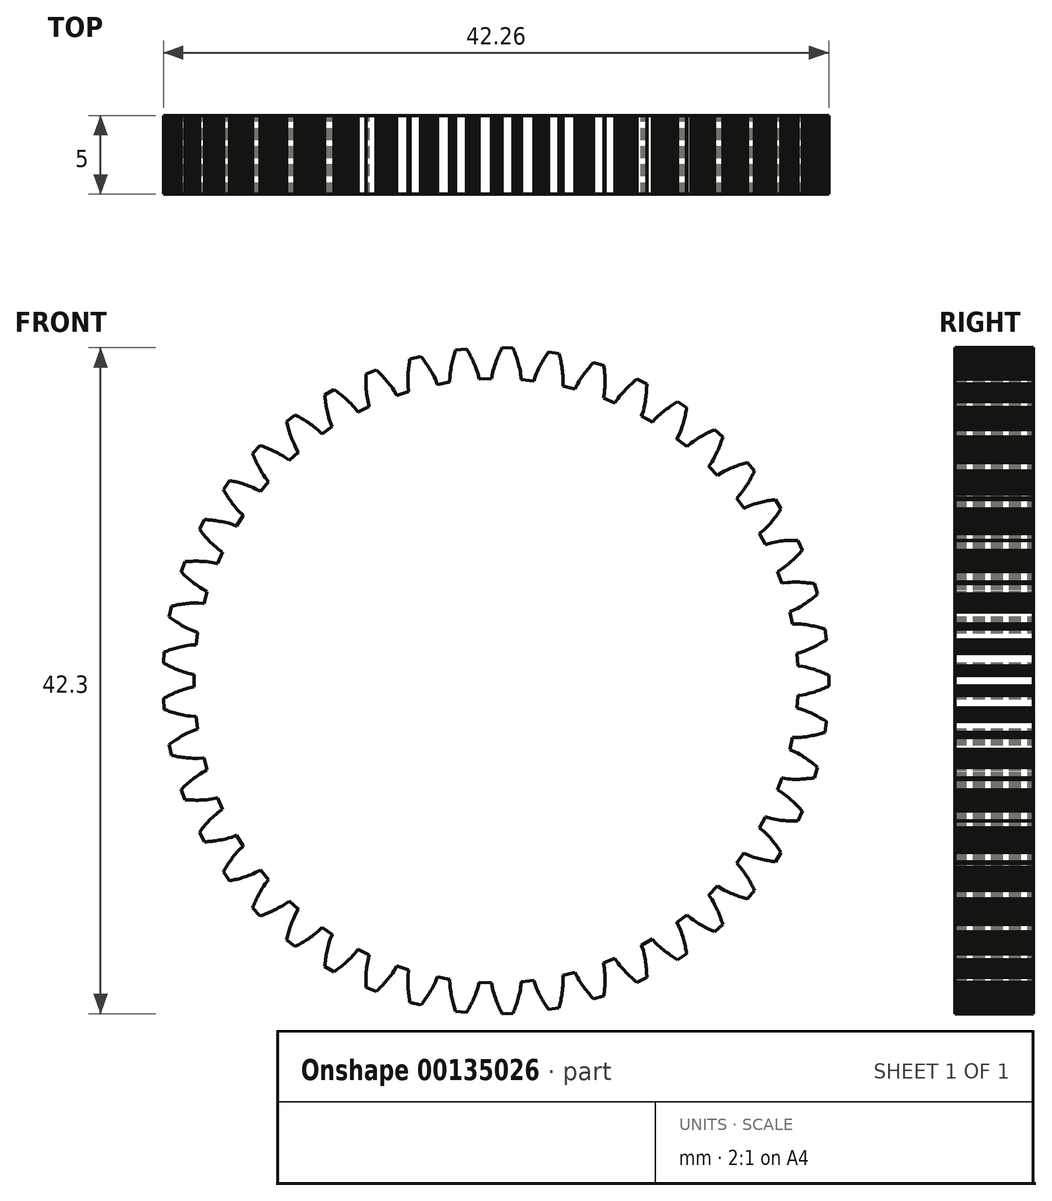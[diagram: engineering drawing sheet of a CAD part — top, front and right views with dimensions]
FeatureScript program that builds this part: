
annotation { "Feature Type Name" : "Feature", "Feature Type Description" : "" }
export const myFeature = defineFeature(function(context is Context, id is Id, definition is map)
    precondition{}
    {
        {
            var Q0;
            Q0=qCreatedBy(makeId("Front.planeOp"),FACE);
            var sketch = newSketch(context, id + "F0", { "sketchPlane" : qUnion([Q0])});
            skLineSegment(sketch, "E0", {"start": v(19.15, -0.94) * mm, "end": v(19.17, -0.94) * mm});
            skLineSegment(sketch, "E1", {"start": v(19.17, -0.94) * mm, "end": v(19.5, -0.9) * mm});
            skLineSegment(sketch, "E2", {"start": v(19.5, -0.9) * mm, "end": v(19.67, -0.86) * mm});
            skLineSegment(sketch, "E3", {"start": v(19.67, -0.86) * mm, "end": v(19.83, -0.82) * mm});
            skLineSegment(sketch, "E4", {"start": v(19.83, -0.82) * mm, "end": v(19.97, -0.78) * mm});
            skLineSegment(sketch, "E5", {"start": v(19.97, -0.78) * mm, "end": v(20.1, -0.74) * mm});
            skLineSegment(sketch, "E6", {"start": v(20.1, -0.74) * mm, "end": v(20.23, -0.7) * mm});
            skLineSegment(sketch, "E7", {"start": v(20.23, -0.7) * mm, "end": v(20.36, -0.66) * mm});
            skLineSegment(sketch, "E8", {"start": v(20.36, -0.66) * mm, "end": v(20.47, -0.62) * mm});
            skLineSegment(sketch, "E9", {"start": v(20.47, -0.62) * mm, "end": v(20.6, -0.58) * mm});
            skLineSegment(sketch, "E10", {"start": v(20.6, -0.58) * mm, "end": v(20.7, -0.53) * mm});
            skLineSegment(sketch, "E11", {"start": v(20.7, -0.53) * mm, "end": v(20.81, -0.49) * mm});
            skLineSegment(sketch, "E12", {"start": v(20.81, -0.49) * mm, "end": v(20.92, -0.44) * mm});
            skLineSegment(sketch, "E13", {"start": v(20.92, -0.44) * mm, "end": v(21.03, -0.4) * mm});
            skLineSegment(sketch, "E14", {"start": v(21.03, -0.4) * mm, "end": v(21.13, -0.35) * mm});
            skLineSegment(sketch, "E15", {"start": v(21.13, -0.35) * mm, "end": v(21.13, 0.35) * mm});
            skLineSegment(sketch, "E16", {"start": v(21.13, 0.35) * mm, "end": v(21.03, 0.4) * mm});
            skLineSegment(sketch, "E17", {"start": v(21.03, 0.4) * mm, "end": v(20.92, 0.44) * mm});
            skLineSegment(sketch, "E18", {"start": v(20.92, 0.44) * mm, "end": v(20.81, 0.49) * mm});
            skLineSegment(sketch, "E19", {"start": v(20.81, 0.49) * mm, "end": v(20.7, 0.53) * mm});
            skLineSegment(sketch, "E20", {"start": v(20.7, 0.53) * mm, "end": v(20.6, 0.58) * mm});
            skLineSegment(sketch, "E21", {"start": v(20.6, 0.58) * mm, "end": v(20.47, 0.62) * mm});
            skLineSegment(sketch, "E22", {"start": v(20.47, 0.62) * mm, "end": v(20.36, 0.66) * mm});
            skLineSegment(sketch, "E23", {"start": v(20.36, 0.66) * mm, "end": v(20.23, 0.7) * mm});
            skLineSegment(sketch, "E24", {"start": v(20.23, 0.7) * mm, "end": v(20.1, 0.74) * mm});
            skLineSegment(sketch, "E25", {"start": v(20.1, 0.74) * mm, "end": v(19.97, 0.78) * mm});
            skLineSegment(sketch, "E26", {"start": v(19.97, 0.78) * mm, "end": v(19.83, 0.82) * mm});
            skLineSegment(sketch, "E27", {"start": v(19.83, 0.82) * mm, "end": v(19.67, 0.86) * mm});
            skLineSegment(sketch, "E28", {"start": v(19.67, 0.86) * mm, "end": v(19.5, 0.9) * mm});
            skLineSegment(sketch, "E29", {"start": v(19.5, 0.9) * mm, "end": v(19.17, 0.94) * mm});
            skLineSegment(sketch, "E30", {"start": v(19.17, 0.94) * mm, "end": v(19.15, 0.94) * mm});
            skLineSegment(sketch, "E31", {"start": v(19.15, 0.94) * mm, "end": v(19.1, 1.74) * mm});
            skLineSegment(sketch, "E32", {"start": v(19.1, 1.74) * mm, "end": v(19.12, 1.74) * mm});
            skLineSegment(sketch, "E33", {"start": v(19.12, 1.74) * mm, "end": v(19.43, 1.83) * mm});
            skLineSegment(sketch, "E34", {"start": v(19.43, 1.83) * mm, "end": v(19.6, 1.89) * mm});
            skLineSegment(sketch, "E35", {"start": v(19.6, 1.89) * mm, "end": v(19.75, 1.95) * mm});
            skLineSegment(sketch, "E36", {"start": v(19.75, 1.95) * mm, "end": v(19.89, 2) * mm});
            skLineSegment(sketch, "E37", {"start": v(19.89, 2) * mm, "end": v(20.01, 2.06) * mm});
            skLineSegment(sketch, "E38", {"start": v(20.01, 2.06) * mm, "end": v(20.13, 2.12) * mm});
            skLineSegment(sketch, "E39", {"start": v(20.13, 2.12) * mm, "end": v(20.25, 2.18) * mm});
            skLineSegment(sketch, "E40", {"start": v(20.25, 2.18) * mm, "end": v(20.36, 2.24) * mm});
            skLineSegment(sketch, "E41", {"start": v(20.36, 2.24) * mm, "end": v(20.47, 2.3) * mm});
            skLineSegment(sketch, "E42", {"start": v(20.47, 2.3) * mm, "end": v(20.58, 2.36) * mm});
            skLineSegment(sketch, "E43", {"start": v(20.58, 2.36) * mm, "end": v(20.68, 2.42) * mm});
            skLineSegment(sketch, "E44", {"start": v(20.68, 2.42) * mm, "end": v(20.78, 2.48) * mm});
            skLineSegment(sketch, "E45", {"start": v(20.78, 2.48) * mm, "end": v(20.88, 2.54) * mm});
            skLineSegment(sketch, "E46", {"start": v(20.88, 2.54) * mm, "end": v(20.98, 2.6) * mm});
            skLineSegment(sketch, "E47", {"start": v(20.98, 2.6) * mm, "end": v(20.88, 3.29) * mm});
            skLineSegment(sketch, "E48", {"start": v(20.88, 3.29) * mm, "end": v(20.77, 3.32) * mm});
            skLineSegment(sketch, "E49", {"start": v(20.77, 3.32) * mm, "end": v(20.66, 3.35) * mm});
            skLineSegment(sketch, "E50", {"start": v(20.66, 3.35) * mm, "end": v(20.54, 3.38) * mm});
            skLineSegment(sketch, "E51", {"start": v(20.54, 3.38) * mm, "end": v(20.43, 3.41) * mm});
            skLineSegment(sketch, "E52", {"start": v(20.43, 3.41) * mm, "end": v(20.3, 3.44) * mm});
            skLineSegment(sketch, "E53", {"start": v(20.3, 3.44) * mm, "end": v(20.19, 3.47) * mm});
            skLineSegment(sketch, "E54", {"start": v(20.19, 3.47) * mm, "end": v(20.07, 3.5) * mm});
            skLineSegment(sketch, "E55", {"start": v(20.07, 3.5) * mm, "end": v(19.94, 3.51) * mm});
            skLineSegment(sketch, "E56", {"start": v(19.94, 3.51) * mm, "end": v(19.8, 3.54) * mm});
            skLineSegment(sketch, "E57", {"start": v(19.8, 3.54) * mm, "end": v(19.67, 3.56) * mm});
            skLineSegment(sketch, "E58", {"start": v(19.67, 3.56) * mm, "end": v(19.52, 3.58) * mm});
            skLineSegment(sketch, "E59", {"start": v(19.52, 3.58) * mm, "end": v(19.36, 3.6) * mm});
            skLineSegment(sketch, "E60", {"start": v(19.36, 3.6) * mm, "end": v(19.18, 3.6) * mm});
            skLineSegment(sketch, "E61", {"start": v(19.18, 3.6) * mm, "end": v(18.85, 3.6) * mm});
            skLineSegment(sketch, "E62", {"start": v(18.85, 3.6) * mm, "end": v(18.84, 3.6) * mm});
            skLineSegment(sketch, "E63", {"start": v(18.84, 3.6) * mm, "end": v(18.67, 4.38) * mm});
            skLineSegment(sketch, "E64", {"start": v(18.67, 4.38) * mm, "end": v(18.69, 4.38) * mm});
            skLineSegment(sketch, "E65", {"start": v(18.69, 4.38) * mm, "end": v(18.99, 4.52) * mm});
            skLineSegment(sketch, "E66", {"start": v(18.99, 4.52) * mm, "end": v(19.15, 4.6) * mm});
            skLineSegment(sketch, "E67", {"start": v(19.15, 4.6) * mm, "end": v(19.29, 4.68) * mm});
            skLineSegment(sketch, "E68", {"start": v(19.29, 4.68) * mm, "end": v(19.41, 4.76) * mm});
            skLineSegment(sketch, "E69", {"start": v(19.41, 4.76) * mm, "end": v(19.53, 4.83) * mm});
            skLineSegment(sketch, "E70", {"start": v(19.53, 4.83) * mm, "end": v(19.64, 4.9) * mm});
            skLineSegment(sketch, "E71", {"start": v(19.64, 4.9) * mm, "end": v(19.75, 4.98) * mm});
            skLineSegment(sketch, "E72", {"start": v(19.75, 4.98) * mm, "end": v(19.85, 5.05) * mm});
            skLineSegment(sketch, "E73", {"start": v(19.85, 5.05) * mm, "end": v(19.95, 5.12) * mm});
            skLineSegment(sketch, "E74", {"start": v(19.95, 5.12) * mm, "end": v(20.05, 5.2) * mm});
            skLineSegment(sketch, "E75", {"start": v(20.05, 5.2) * mm, "end": v(20.14, 5.27) * mm});
            skLineSegment(sketch, "E76", {"start": v(20.14, 5.27) * mm, "end": v(20.23, 5.35) * mm});
            skLineSegment(sketch, "E77", {"start": v(20.23, 5.35) * mm, "end": v(20.32, 5.42) * mm});
            skLineSegment(sketch, "E78", {"start": v(20.32, 5.42) * mm, "end": v(20.4, 5.5) * mm});
            skLineSegment(sketch, "E79", {"start": v(20.4, 5.5) * mm, "end": v(20.22, 6.16) * mm});
            skLineSegment(sketch, "E80", {"start": v(20.22, 6.16) * mm, "end": v(20.1, 6.18) * mm});
            skLineSegment(sketch, "E81", {"start": v(20.1, 6.18) * mm, "end": v(20, 6.2) * mm});
            skLineSegment(sketch, "E82", {"start": v(20, 6.2) * mm, "end": v(19.87, 6.2) * mm});
            skLineSegment(sketch, "E83", {"start": v(19.87, 6.2) * mm, "end": v(19.75, 6.22) * mm});
            skLineSegment(sketch, "E84", {"start": v(19.75, 6.22) * mm, "end": v(19.63, 6.23) * mm});
            skLineSegment(sketch, "E85", {"start": v(19.63, 6.23) * mm, "end": v(19.5, 6.24) * mm});
            skLineSegment(sketch, "E86", {"start": v(19.5, 6.24) * mm, "end": v(19.38, 6.25) * mm});
            skLineSegment(sketch, "E87", {"start": v(19.38, 6.25) * mm, "end": v(19.25, 6.26) * mm});
            skLineSegment(sketch, "E88", {"start": v(19.25, 6.26) * mm, "end": v(19.12, 6.26) * mm});
            skLineSegment(sketch, "E89", {"start": v(19.12, 6.26) * mm, "end": v(18.98, 6.26) * mm});
            skLineSegment(sketch, "E90", {"start": v(18.98, 6.26) * mm, "end": v(18.83, 6.26) * mm});
            skLineSegment(sketch, "E91", {"start": v(18.83, 6.26) * mm, "end": v(18.67, 6.25) * mm});
            skLineSegment(sketch, "E92", {"start": v(18.67, 6.25) * mm, "end": v(18.5, 6.24) * mm});
            skLineSegment(sketch, "E93", {"start": v(18.5, 6.24) * mm, "end": v(18.17, 6.2) * mm});
            skLineSegment(sketch, "E94", {"start": v(18.17, 6.2) * mm, "end": v(18.15, 6.19) * mm});
            skLineSegment(sketch, "E95", {"start": v(18.15, 6.19) * mm, "end": v(17.88, 6.94) * mm});
            skLineSegment(sketch, "E96", {"start": v(17.88, 6.94) * mm, "end": v(17.9, 6.94) * mm});
            skLineSegment(sketch, "E97", {"start": v(17.9, 6.94) * mm, "end": v(18.17, 7.12) * mm});
            skLineSegment(sketch, "E98", {"start": v(18.17, 7.12) * mm, "end": v(18.32, 7.22) * mm});
            skLineSegment(sketch, "E99", {"start": v(18.32, 7.22) * mm, "end": v(18.45, 7.32) * mm});
            skLineSegment(sketch, "E100", {"start": v(18.45, 7.32) * mm, "end": v(18.56, 7.41) * mm});
            skLineSegment(sketch, "E101", {"start": v(18.56, 7.41) * mm, "end": v(18.67, 7.5) * mm});
            skLineSegment(sketch, "E102", {"start": v(18.67, 7.5) * mm, "end": v(18.77, 7.6) * mm});
            skLineSegment(sketch, "E103", {"start": v(18.77, 7.6) * mm, "end": v(18.86, 7.68) * mm});
            skLineSegment(sketch, "E104", {"start": v(18.86, 7.68) * mm, "end": v(18.96, 7.77) * mm});
            skLineSegment(sketch, "E105", {"start": v(18.96, 7.77) * mm, "end": v(19.04, 7.85) * mm});
            skLineSegment(sketch, "E106", {"start": v(19.04, 7.85) * mm, "end": v(19.13, 7.94) * mm});
            skLineSegment(sketch, "E107", {"start": v(19.13, 7.94) * mm, "end": v(19.21, 8.03) * mm});
            skLineSegment(sketch, "E108", {"start": v(19.21, 8.03) * mm, "end": v(19.3, 8.11) * mm});
            skLineSegment(sketch, "E109", {"start": v(19.3, 8.11) * mm, "end": v(19.37, 8.2) * mm});
            skLineSegment(sketch, "E110", {"start": v(19.37, 8.2) * mm, "end": v(19.45, 8.29) * mm});
            skLineSegment(sketch, "E111", {"start": v(19.45, 8.29) * mm, "end": v(19.16, 8.92) * mm});
            skLineSegment(sketch, "E112", {"start": v(19.16, 8.92) * mm, "end": v(19.05, 8.92) * mm});
            skLineSegment(sketch, "E113", {"start": v(19.05, 8.92) * mm, "end": v(18.93, 8.92) * mm});
            skLineSegment(sketch, "E114", {"start": v(18.93, 8.92) * mm, "end": v(18.82, 8.92) * mm});
            skLineSegment(sketch, "E115", {"start": v(18.82, 8.92) * mm, "end": v(18.7, 8.91) * mm});
            skLineSegment(sketch, "E116", {"start": v(18.7, 8.91) * mm, "end": v(18.57, 8.9) * mm});
            skLineSegment(sketch, "E117", {"start": v(18.57, 8.9) * mm, "end": v(18.45, 8.9) * mm});
            skLineSegment(sketch, "E118", {"start": v(18.45, 8.9) * mm, "end": v(18.32, 8.9) * mm});
            skLineSegment(sketch, "E119", {"start": v(18.32, 8.9) * mm, "end": v(18.2, 8.88) * mm});
            skLineSegment(sketch, "E120", {"start": v(18.2, 8.88) * mm, "end": v(18.06, 8.86) * mm});
            skLineSegment(sketch, "E121", {"start": v(18.06, 8.86) * mm, "end": v(17.92, 8.84) * mm});
            skLineSegment(sketch, "E122", {"start": v(17.92, 8.84) * mm, "end": v(17.78, 8.82) * mm});
            skLineSegment(sketch, "E123", {"start": v(17.78, 8.82) * mm, "end": v(17.62, 8.8) * mm});
            skLineSegment(sketch, "E124", {"start": v(17.62, 8.8) * mm, "end": v(17.44, 8.75) * mm});
            skLineSegment(sketch, "E125", {"start": v(17.44, 8.75) * mm, "end": v(17.13, 8.66) * mm});
            skLineSegment(sketch, "E126", {"start": v(17.13, 8.66) * mm, "end": v(17.11, 8.65) * mm});
            skLineSegment(sketch, "E127", {"start": v(17.11, 8.65) * mm, "end": v(16.74, 9.36) * mm});
            skLineSegment(sketch, "E128", {"start": v(16.74, 9.36) * mm, "end": v(16.75, 9.37) * mm});
            skLineSegment(sketch, "E129", {"start": v(16.75, 9.37) * mm, "end": v(17, 9.58) * mm});
            skLineSegment(sketch, "E130", {"start": v(17, 9.58) * mm, "end": v(17.14, 9.7) * mm});
            skLineSegment(sketch, "E131", {"start": v(17.14, 9.7) * mm, "end": v(17.25, 9.82) * mm});
            skLineSegment(sketch, "E132", {"start": v(17.25, 9.82) * mm, "end": v(17.35, 9.93) * mm});
            skLineSegment(sketch, "E133", {"start": v(17.35, 9.93) * mm, "end": v(17.44, 10.03) * mm});
            skLineSegment(sketch, "E134", {"start": v(17.44, 10.03) * mm, "end": v(17.53, 10.13) * mm});
            skLineSegment(sketch, "E135", {"start": v(17.53, 10.13) * mm, "end": v(17.61, 10.23) * mm});
            skLineSegment(sketch, "E136", {"start": v(17.61, 10.23) * mm, "end": v(17.69, 10.33) * mm});
            skLineSegment(sketch, "E137", {"start": v(17.69, 10.33) * mm, "end": v(17.77, 10.43) * mm});
            skLineSegment(sketch, "E138", {"start": v(17.77, 10.43) * mm, "end": v(17.84, 10.53) * mm});
            skLineSegment(sketch, "E139", {"start": v(17.84, 10.53) * mm, "end": v(17.9, 10.62) * mm});
            skLineSegment(sketch, "E140", {"start": v(17.9, 10.62) * mm, "end": v(17.97, 10.72) * mm});
            skLineSegment(sketch, "E141", {"start": v(17.97, 10.72) * mm, "end": v(18.04, 10.82) * mm});
            skLineSegment(sketch, "E142", {"start": v(18.04, 10.82) * mm, "end": v(18.1, 10.91) * mm});
            skLineSegment(sketch, "E143", {"start": v(18.1, 10.91) * mm, "end": v(17.74, 11.5) * mm});
            skLineSegment(sketch, "E144", {"start": v(17.74, 11.5) * mm, "end": v(17.62, 11.48) * mm});
            skLineSegment(sketch, "E145", {"start": v(17.62, 11.48) * mm, "end": v(17.5, 11.47) * mm});
            skLineSegment(sketch, "E146", {"start": v(17.5, 11.47) * mm, "end": v(17.4, 11.45) * mm});
            skLineSegment(sketch, "E147", {"start": v(17.4, 11.45) * mm, "end": v(17.27, 11.43) * mm});
            skLineSegment(sketch, "E148", {"start": v(17.27, 11.43) * mm, "end": v(17.15, 11.4) * mm});
            skLineSegment(sketch, "E149", {"start": v(17.15, 11.4) * mm, "end": v(17.03, 11.38) * mm});
            skLineSegment(sketch, "E150", {"start": v(17.03, 11.38) * mm, "end": v(16.9, 11.36) * mm});
            skLineSegment(sketch, "E151", {"start": v(16.9, 11.36) * mm, "end": v(16.78, 11.33) * mm});
            skLineSegment(sketch, "E152", {"start": v(16.78, 11.33) * mm, "end": v(16.65, 11.3) * mm});
            skLineSegment(sketch, "E153", {"start": v(16.65, 11.3) * mm, "end": v(16.52, 11.25) * mm});
            skLineSegment(sketch, "E154", {"start": v(16.52, 11.25) * mm, "end": v(16.38, 11.21) * mm});
            skLineSegment(sketch, "E155", {"start": v(16.38, 11.21) * mm, "end": v(16.23, 11.16) * mm});
            skLineSegment(sketch, "E156", {"start": v(16.23, 11.16) * mm, "end": v(16.06, 11.1) * mm});
            skLineSegment(sketch, "E157", {"start": v(16.06, 11.1) * mm, "end": v(15.76, 10.96) * mm});
            skLineSegment(sketch, "E158", {"start": v(15.76, 10.96) * mm, "end": v(15.74, 10.95) * mm});
            skLineSegment(sketch, "E159", {"start": v(15.74, 10.95) * mm, "end": v(15.27, 11.6) * mm});
            skLineSegment(sketch, "E160", {"start": v(15.27, 11.6) * mm, "end": v(15.29, 11.61) * mm});
            skLineSegment(sketch, "E161", {"start": v(15.29, 11.61) * mm, "end": v(15.5, 11.85) * mm});
            skLineSegment(sketch, "E162", {"start": v(15.5, 11.85) * mm, "end": v(15.62, 12) * mm});
            skLineSegment(sketch, "E163", {"start": v(15.62, 12) * mm, "end": v(15.71, 12.13) * mm});
            skLineSegment(sketch, "E164", {"start": v(15.71, 12.13) * mm, "end": v(15.8, 12.25) * mm});
            skLineSegment(sketch, "E165", {"start": v(15.8, 12.25) * mm, "end": v(15.88, 12.36) * mm});
            skLineSegment(sketch, "E166", {"start": v(15.88, 12.36) * mm, "end": v(15.95, 12.47) * mm});
            skLineSegment(sketch, "E167", {"start": v(15.95, 12.47) * mm, "end": v(16.02, 12.59) * mm});
            skLineSegment(sketch, "E168", {"start": v(16.02, 12.59) * mm, "end": v(16.08, 12.7) * mm});
            skLineSegment(sketch, "E169", {"start": v(16.08, 12.7) * mm, "end": v(16.14, 12.8) * mm});
            skLineSegment(sketch, "E170", {"start": v(16.14, 12.8) * mm, "end": v(16.2, 12.9) * mm});
            skLineSegment(sketch, "E171", {"start": v(16.2, 12.9) * mm, "end": v(16.25, 13.01) * mm});
            skLineSegment(sketch, "E172", {"start": v(16.25, 13.01) * mm, "end": v(16.3, 13.12) * mm});
            skLineSegment(sketch, "E173", {"start": v(16.3, 13.12) * mm, "end": v(16.36, 13.22) * mm});
            skLineSegment(sketch, "E174", {"start": v(16.36, 13.22) * mm, "end": v(16.4, 13.33) * mm});
            skLineSegment(sketch, "E175", {"start": v(16.4, 13.33) * mm, "end": v(15.96, 13.86) * mm});
            skLineSegment(sketch, "E176", {"start": v(15.96, 13.86) * mm, "end": v(15.85, 13.83) * mm});
            skLineSegment(sketch, "E177", {"start": v(15.85, 13.83) * mm, "end": v(15.74, 13.8) * mm});
            skLineSegment(sketch, "E178", {"start": v(15.74, 13.8) * mm, "end": v(15.63, 13.76) * mm});
            skLineSegment(sketch, "E179", {"start": v(15.63, 13.76) * mm, "end": v(15.51, 13.72) * mm});
            skLineSegment(sketch, "E180", {"start": v(15.51, 13.72) * mm, "end": v(15.4, 13.69) * mm});
            skLineSegment(sketch, "E181", {"start": v(15.4, 13.69) * mm, "end": v(15.28, 13.64) * mm});
            skLineSegment(sketch, "E182", {"start": v(15.28, 13.64) * mm, "end": v(15.16, 13.6) * mm});
            skLineSegment(sketch, "E183", {"start": v(15.16, 13.6) * mm, "end": v(15.04, 13.55) * mm});
            skLineSegment(sketch, "E184", {"start": v(15.04, 13.55) * mm, "end": v(14.92, 13.5) * mm});
            skLineSegment(sketch, "E185", {"start": v(14.92, 13.5) * mm, "end": v(14.8, 13.45) * mm});
            skLineSegment(sketch, "E186", {"start": v(14.8, 13.45) * mm, "end": v(14.66, 13.38) * mm});
            skLineSegment(sketch, "E187", {"start": v(14.66, 13.38) * mm, "end": v(14.52, 13.31) * mm});
            skLineSegment(sketch, "E188", {"start": v(14.52, 13.31) * mm, "end": v(14.36, 13.23) * mm});
            skLineSegment(sketch, "E189", {"start": v(14.36, 13.23) * mm, "end": v(14.08, 13.05) * mm});
            skLineSegment(sketch, "E190", {"start": v(14.08, 13.05) * mm, "end": v(14.07, 13.04) * mm});
            skLineSegment(sketch, "E191", {"start": v(14.07, 13.04) * mm, "end": v(13.5, 13.62) * mm});
            skLineSegment(sketch, "E192", {"start": v(13.5, 13.62) * mm, "end": v(13.52, 13.63) * mm});
            skLineSegment(sketch, "E193", {"start": v(13.52, 13.63) * mm, "end": v(13.7, 13.9) * mm});
            skLineSegment(sketch, "E194", {"start": v(13.7, 13.9) * mm, "end": v(13.8, 14.06) * mm});
            skLineSegment(sketch, "E195", {"start": v(13.8, 14.06) * mm, "end": v(13.87, 14.2) * mm});
            skLineSegment(sketch, "E196", {"start": v(13.87, 14.2) * mm, "end": v(13.94, 14.33) * mm});
            skLineSegment(sketch, "E197", {"start": v(13.94, 14.33) * mm, "end": v(14, 14.45) * mm});
            skLineSegment(sketch, "E198", {"start": v(14, 14.45) * mm, "end": v(14.06, 14.57) * mm});
            skLineSegment(sketch, "E199", {"start": v(14.06, 14.57) * mm, "end": v(14.1, 14.7) * mm});
            skLineSegment(sketch, "E200", {"start": v(14.1, 14.7) * mm, "end": v(14.16, 14.81) * mm});
            skLineSegment(sketch, "E201", {"start": v(14.16, 14.81) * mm, "end": v(14.2, 14.93) * mm});
            skLineSegment(sketch, "E202", {"start": v(14.2, 14.93) * mm, "end": v(14.24, 15.04) * mm});
            skLineSegment(sketch, "E203", {"start": v(14.24, 15.04) * mm, "end": v(14.28, 15.15) * mm});
            skLineSegment(sketch, "E204", {"start": v(14.28, 15.15) * mm, "end": v(14.32, 15.26) * mm});
            skLineSegment(sketch, "E205", {"start": v(14.32, 15.26) * mm, "end": v(14.36, 15.37) * mm});
            skLineSegment(sketch, "E206", {"start": v(14.36, 15.37) * mm, "end": v(14.4, 15.48) * mm});
            skLineSegment(sketch, "E207", {"start": v(14.4, 15.48) * mm, "end": v(13.88, 15.95) * mm});
            skLineSegment(sketch, "E208", {"start": v(13.88, 15.95) * mm, "end": v(13.77, 15.9) * mm});
            skLineSegment(sketch, "E209", {"start": v(13.77, 15.9) * mm, "end": v(13.67, 15.85) * mm});
            skLineSegment(sketch, "E210", {"start": v(13.67, 15.85) * mm, "end": v(13.56, 15.8) * mm});
            skLineSegment(sketch, "E211", {"start": v(13.56, 15.8) * mm, "end": v(13.45, 15.75) * mm});
            skLineSegment(sketch, "E212", {"start": v(13.45, 15.75) * mm, "end": v(13.34, 15.7) * mm});
            skLineSegment(sketch, "E213", {"start": v(13.34, 15.7) * mm, "end": v(13.23, 15.64) * mm});
            skLineSegment(sketch, "E214", {"start": v(13.23, 15.64) * mm, "end": v(13.12, 15.58) * mm});
            skLineSegment(sketch, "E215", {"start": v(13.12, 15.58) * mm, "end": v(13.01, 15.52) * mm});
            skLineSegment(sketch, "E216", {"start": v(13.01, 15.52) * mm, "end": v(12.9, 15.45) * mm});
            skLineSegment(sketch, "E217", {"start": v(12.9, 15.45) * mm, "end": v(12.78, 15.38) * mm});
            skLineSegment(sketch, "E218", {"start": v(12.78, 15.38) * mm, "end": v(12.65, 15.3) * mm});
            skLineSegment(sketch, "E219", {"start": v(12.65, 15.3) * mm, "end": v(12.52, 15.2) * mm});
            skLineSegment(sketch, "E220", {"start": v(12.52, 15.2) * mm, "end": v(12.37, 15.1) * mm});
            skLineSegment(sketch, "E221", {"start": v(12.37, 15.1) * mm, "end": v(12.13, 14.89) * mm});
            skLineSegment(sketch, "E222", {"start": v(12.13, 14.89) * mm, "end": v(12.11, 14.87) * mm});
            skLineSegment(sketch, "E223", {"start": v(12.11, 14.87) * mm, "end": v(11.48, 15.36) * mm});
            skLineSegment(sketch, "E224", {"start": v(11.48, 15.36) * mm, "end": v(11.5, 15.38) * mm});
            skLineSegment(sketch, "E225", {"start": v(11.5, 15.38) * mm, "end": v(11.64, 15.67) * mm});
            skLineSegment(sketch, "E226", {"start": v(11.64, 15.67) * mm, "end": v(11.7, 15.84) * mm});
            skLineSegment(sketch, "E227", {"start": v(11.7, 15.84) * mm, "end": v(11.76, 16) * mm});
            skLineSegment(sketch, "E228", {"start": v(11.76, 16) * mm, "end": v(11.81, 16.13) * mm});
            skLineSegment(sketch, "E229", {"start": v(11.81, 16.13) * mm, "end": v(11.85, 16.26) * mm});
            skLineSegment(sketch, "E230", {"start": v(11.85, 16.26) * mm, "end": v(11.9, 16.4) * mm});
            skLineSegment(sketch, "E231", {"start": v(11.9, 16.4) * mm, "end": v(11.93, 16.52) * mm});
            skLineSegment(sketch, "E232", {"start": v(11.93, 16.52) * mm, "end": v(11.96, 16.64) * mm});
            skLineSegment(sketch, "E233", {"start": v(11.96, 16.64) * mm, "end": v(11.99, 16.76) * mm});
            skLineSegment(sketch, "E234", {"start": v(11.99, 16.76) * mm, "end": v(12.01, 16.88) * mm});
            skLineSegment(sketch, "E235", {"start": v(12.01, 16.88) * mm, "end": v(12.04, 17) * mm});
            skLineSegment(sketch, "E236", {"start": v(12.04, 17) * mm, "end": v(12.06, 17.11) * mm});
            skLineSegment(sketch, "E237", {"start": v(12.06, 17.11) * mm, "end": v(12.08, 17.23) * mm});
            skLineSegment(sketch, "E238", {"start": v(12.08, 17.23) * mm, "end": v(12.1, 17.34) * mm});
            skLineSegment(sketch, "E239", {"start": v(12.1, 17.34) * mm, "end": v(11.53, 17.73) * mm});
            skLineSegment(sketch, "E240", {"start": v(11.53, 17.73) * mm, "end": v(11.43, 17.67) * mm});
            skLineSegment(sketch, "E241", {"start": v(11.43, 17.67) * mm, "end": v(11.33, 17.6) * mm});
            skLineSegment(sketch, "E242", {"start": v(11.33, 17.6) * mm, "end": v(11.23, 17.54) * mm});
            skLineSegment(sketch, "E243", {"start": v(11.23, 17.54) * mm, "end": v(11.13, 17.47) * mm});
            skLineSegment(sketch, "E244", {"start": v(11.13, 17.47) * mm, "end": v(11.03, 17.4) * mm});
            skLineSegment(sketch, "E245", {"start": v(11.03, 17.4) * mm, "end": v(10.93, 17.33) * mm});
            skLineSegment(sketch, "E246", {"start": v(10.93, 17.33) * mm, "end": v(10.83, 17.26) * mm});
            skLineSegment(sketch, "E247", {"start": v(10.83, 17.26) * mm, "end": v(10.72, 17.18) * mm});
            skLineSegment(sketch, "E248", {"start": v(10.72, 17.18) * mm, "end": v(10.62, 17.1) * mm});
            skLineSegment(sketch, "E249", {"start": v(10.62, 17.1) * mm, "end": v(10.51, 17) * mm});
            skLineSegment(sketch, "E250", {"start": v(10.51, 17) * mm, "end": v(10.4, 16.9) * mm});
            skLineSegment(sketch, "E251", {"start": v(10.4, 16.9) * mm, "end": v(10.28, 16.8) * mm});
            skLineSegment(sketch, "E252", {"start": v(10.28, 16.8) * mm, "end": v(10.15, 16.67) * mm});
            skLineSegment(sketch, "E253", {"start": v(10.15, 16.67) * mm, "end": v(9.94, 16.43) * mm});
            skLineSegment(sketch, "E254", {"start": v(9.94, 16.43) * mm, "end": v(9.93, 16.41) * mm});
            skLineSegment(sketch, "E255", {"start": v(9.93, 16.41) * mm, "end": v(9.23, 16.82) * mm});
            skLineSegment(sketch, "E256", {"start": v(9.23, 16.82) * mm, "end": v(9.24, 16.83) * mm});
            skLineSegment(sketch, "E257", {"start": v(9.24, 16.83) * mm, "end": v(9.34, 17.14) * mm});
            skLineSegment(sketch, "E258", {"start": v(9.34, 17.14) * mm, "end": v(9.39, 17.32) * mm});
            skLineSegment(sketch, "E259", {"start": v(9.39, 17.32) * mm, "end": v(9.42, 17.47) * mm});
            skLineSegment(sketch, "E260", {"start": v(9.42, 17.47) * mm, "end": v(9.45, 17.62) * mm});
            skLineSegment(sketch, "E261", {"start": v(9.45, 17.62) * mm, "end": v(9.47, 17.76) * mm});
            skLineSegment(sketch, "E262", {"start": v(9.47, 17.76) * mm, "end": v(9.5, 17.89) * mm});
            skLineSegment(sketch, "E263", {"start": v(9.5, 17.89) * mm, "end": v(9.51, 18.02) * mm});
            skLineSegment(sketch, "E264", {"start": v(9.51, 18.02) * mm, "end": v(9.53, 18.14) * mm});
            skLineSegment(sketch, "E265", {"start": v(9.53, 18.14) * mm, "end": v(9.54, 18.27) * mm});
            skLineSegment(sketch, "E266", {"start": v(9.54, 18.27) * mm, "end": v(9.55, 18.39) * mm});
            skLineSegment(sketch, "E267", {"start": v(9.55, 18.39) * mm, "end": v(9.55, 18.5) * mm});
            skLineSegment(sketch, "E268", {"start": v(9.55, 18.5) * mm, "end": v(9.56, 18.62) * mm});
            skLineSegment(sketch, "E269", {"start": v(9.56, 18.62) * mm, "end": v(9.56, 18.74) * mm});
            skLineSegment(sketch, "E270", {"start": v(9.56, 18.74) * mm, "end": v(9.57, 18.86) * mm});
            skLineSegment(sketch, "E271", {"start": v(9.57, 18.86) * mm, "end": v(8.95, 19.16) * mm});
            skLineSegment(sketch, "E272", {"start": v(8.95, 19.16) * mm, "end": v(8.86, 19.09) * mm});
            skLineSegment(sketch, "E273", {"start": v(8.86, 19.09) * mm, "end": v(8.77, 19.01) * mm});
            skLineSegment(sketch, "E274", {"start": v(8.77, 19.01) * mm, "end": v(8.68, 18.93) * mm});
            skLineSegment(sketch, "E275", {"start": v(8.68, 18.93) * mm, "end": v(8.59, 18.85) * mm});
            skLineSegment(sketch, "E276", {"start": v(8.59, 18.85) * mm, "end": v(8.5, 18.77) * mm});
            skLineSegment(sketch, "E277", {"start": v(8.5, 18.77) * mm, "end": v(8.41, 18.69) * mm});
            skLineSegment(sketch, "E278", {"start": v(8.41, 18.69) * mm, "end": v(8.32, 18.6) * mm});
            skLineSegment(sketch, "E279", {"start": v(8.32, 18.6) * mm, "end": v(8.23, 18.5) * mm});
            skLineSegment(sketch, "E280", {"start": v(8.23, 18.5) * mm, "end": v(8.14, 18.4) * mm});
            skLineSegment(sketch, "E281", {"start": v(8.14, 18.4) * mm, "end": v(8.04, 18.3) * mm});
            skLineSegment(sketch, "E282", {"start": v(8.04, 18.3) * mm, "end": v(7.95, 18.2) * mm});
            skLineSegment(sketch, "E283", {"start": v(7.95, 18.2) * mm, "end": v(7.85, 18.07) * mm});
            skLineSegment(sketch, "E284", {"start": v(7.85, 18.07) * mm, "end": v(7.73, 17.93) * mm});
            skLineSegment(sketch, "E285", {"start": v(7.73, 17.93) * mm, "end": v(7.55, 17.66) * mm});
            skLineSegment(sketch, "E286", {"start": v(7.55, 17.66) * mm, "end": v(7.54, 17.64) * mm});
            skLineSegment(sketch, "E287", {"start": v(7.54, 17.64) * mm, "end": v(6.8, 17.94) * mm});
            skLineSegment(sketch, "E288", {"start": v(6.8, 17.94) * mm, "end": v(6.8, 17.96) * mm});
            skLineSegment(sketch, "E289", {"start": v(6.8, 17.96) * mm, "end": v(6.87, 18.28) * mm});
            skLineSegment(sketch, "E290", {"start": v(6.87, 18.28) * mm, "end": v(6.89, 18.46) * mm});
            skLineSegment(sketch, "E291", {"start": v(6.89, 18.46) * mm, "end": v(6.9, 18.62) * mm});
            skLineSegment(sketch, "E292", {"start": v(6.9, 18.62) * mm, "end": v(6.9, 18.76) * mm});
            skLineSegment(sketch, "E293", {"start": v(6.9, 18.76) * mm, "end": v(6.91, 18.9) * mm});
            skLineSegment(sketch, "E294", {"start": v(6.91, 18.9) * mm, "end": v(6.91, 19.04) * mm});
            skLineSegment(sketch, "E295", {"start": v(6.91, 19.04) * mm, "end": v(6.91, 19.17) * mm});
            skLineSegment(sketch, "E296", {"start": v(6.91, 19.17) * mm, "end": v(6.9, 19.3) * mm});
            skLineSegment(sketch, "E297", {"start": v(6.9, 19.3) * mm, "end": v(6.9, 19.42) * mm});
            skLineSegment(sketch, "E298", {"start": v(6.9, 19.42) * mm, "end": v(6.9, 19.54) * mm});
            skLineSegment(sketch, "E299", {"start": v(6.9, 19.54) * mm, "end": v(6.89, 19.66) * mm});
            skLineSegment(sketch, "E300", {"start": v(6.89, 19.66) * mm, "end": v(6.88, 19.78) * mm});
            skLineSegment(sketch, "E301", {"start": v(6.88, 19.78) * mm, "end": v(6.86, 19.9) * mm});
            skLineSegment(sketch, "E302", {"start": v(6.86, 19.9) * mm, "end": v(6.85, 20) * mm});
            skLineSegment(sketch, "E303", {"start": v(6.85, 20) * mm, "end": v(6.2, 20.22) * mm});
            skLineSegment(sketch, "E304", {"start": v(6.2, 20.22) * mm, "end": v(6.11, 20.13) * mm});
            skLineSegment(sketch, "E305", {"start": v(6.11, 20.13) * mm, "end": v(6.04, 20.05) * mm});
            skLineSegment(sketch, "E306", {"start": v(6.04, 20.05) * mm, "end": v(5.96, 19.96) * mm});
            skLineSegment(sketch, "E307", {"start": v(5.96, 19.96) * mm, "end": v(5.88, 19.87) * mm});
            skLineSegment(sketch, "E308", {"start": v(5.88, 19.87) * mm, "end": v(5.8, 19.77) * mm});
            skLineSegment(sketch, "E309", {"start": v(5.8, 19.77) * mm, "end": v(5.73, 19.68) * mm});
            skLineSegment(sketch, "E310", {"start": v(5.73, 19.68) * mm, "end": v(5.65, 19.58) * mm});
            skLineSegment(sketch, "E311", {"start": v(5.65, 19.58) * mm, "end": v(5.57, 19.47) * mm});
            skLineSegment(sketch, "E312", {"start": v(5.57, 19.47) * mm, "end": v(5.5, 19.36) * mm});
            skLineSegment(sketch, "E313", {"start": v(5.5, 19.36) * mm, "end": v(5.42, 19.25) * mm});
            skLineSegment(sketch, "E314", {"start": v(5.42, 19.25) * mm, "end": v(5.34, 19.13) * mm});
            skLineSegment(sketch, "E315", {"start": v(5.34, 19.13) * mm, "end": v(5.25, 18.99) * mm});
            skLineSegment(sketch, "E316", {"start": v(5.25, 18.99) * mm, "end": v(5.16, 18.83) * mm});
            skLineSegment(sketch, "E317", {"start": v(5.16, 18.83) * mm, "end": v(5.02, 18.54) * mm});
            skLineSegment(sketch, "E318", {"start": v(5.02, 18.54) * mm, "end": v(5.02, 18.52) * mm});
            skLineSegment(sketch, "E319", {"start": v(5.02, 18.52) * mm, "end": v(4.24, 18.71) * mm});
            skLineSegment(sketch, "E320", {"start": v(4.24, 18.71) * mm, "end": v(4.24, 18.73) * mm});
            skLineSegment(sketch, "E321", {"start": v(4.24, 18.73) * mm, "end": v(4.26, 19.06) * mm});
            skLineSegment(sketch, "E322", {"start": v(4.26, 19.06) * mm, "end": v(4.25, 19.24) * mm});
            skLineSegment(sketch, "E323", {"start": v(4.25, 19.24) * mm, "end": v(4.24, 19.4) * mm});
            skLineSegment(sketch, "E324", {"start": v(4.24, 19.4) * mm, "end": v(4.23, 19.54) * mm});
            skLineSegment(sketch, "E325", {"start": v(4.23, 19.54) * mm, "end": v(4.21, 19.68) * mm});
            skLineSegment(sketch, "E326", {"start": v(4.21, 19.68) * mm, "end": v(4.2, 19.82) * mm});
            skLineSegment(sketch, "E327", {"start": v(4.2, 19.82) * mm, "end": v(4.18, 19.94) * mm});
            skLineSegment(sketch, "E328", {"start": v(4.18, 19.94) * mm, "end": v(4.15, 20.07) * mm});
            skLineSegment(sketch, "E329", {"start": v(4.15, 20.07) * mm, "end": v(4.13, 20.2) * mm});
            skLineSegment(sketch, "E330", {"start": v(4.13, 20.2) * mm, "end": v(4.1, 20.31) * mm});
            skLineSegment(sketch, "E331", {"start": v(4.1, 20.31) * mm, "end": v(4.08, 20.43) * mm});
            skLineSegment(sketch, "E332", {"start": v(4.08, 20.43) * mm, "end": v(4.06, 20.54) * mm});
            skLineSegment(sketch, "E333", {"start": v(4.06, 20.54) * mm, "end": v(4.03, 20.65) * mm});
            skLineSegment(sketch, "E334", {"start": v(4.03, 20.65) * mm, "end": v(4, 20.77) * mm});
            skLineSegment(sketch, "E335", {"start": v(4, 20.77) * mm, "end": v(3.32, 20.89) * mm});
            skLineSegment(sketch, "E336", {"start": v(3.32, 20.89) * mm, "end": v(3.25, 20.8) * mm});
            skLineSegment(sketch, "E337", {"start": v(3.25, 20.8) * mm, "end": v(3.19, 20.7) * mm});
            skLineSegment(sketch, "E338", {"start": v(3.19, 20.7) * mm, "end": v(3.12, 20.6) * mm});
            skLineSegment(sketch, "E339", {"start": v(3.12, 20.6) * mm, "end": v(3.06, 20.5) * mm});
            skLineSegment(sketch, "E340", {"start": v(3.06, 20.5) * mm, "end": v(3, 20.4) * mm});
            skLineSegment(sketch, "E341", {"start": v(3, 20.4) * mm, "end": v(2.93, 20.28) * mm});
            skLineSegment(sketch, "E342", {"start": v(2.93, 20.28) * mm, "end": v(2.87, 20.17) * mm});
            skLineSegment(sketch, "E343", {"start": v(2.87, 20.17) * mm, "end": v(2.8, 20.06) * mm});
            skLineSegment(sketch, "E344", {"start": v(2.8, 20.06) * mm, "end": v(2.75, 19.94) * mm});
            skLineSegment(sketch, "E345", {"start": v(2.75, 19.94) * mm, "end": v(2.69, 19.82) * mm});
            skLineSegment(sketch, "E346", {"start": v(2.69, 19.82) * mm, "end": v(2.62, 19.68) * mm});
            skLineSegment(sketch, "E347", {"start": v(2.62, 19.68) * mm, "end": v(2.56, 19.54) * mm});
            skLineSegment(sketch, "E348", {"start": v(2.56, 19.54) * mm, "end": v(2.5, 19.37) * mm});
            skLineSegment(sketch, "E349", {"start": v(2.5, 19.37) * mm, "end": v(2.4, 19.06) * mm});
            skLineSegment(sketch, "E350", {"start": v(2.4, 19.06) * mm, "end": v(2.39, 19.04) * mm});
            skLineSegment(sketch, "E351", {"start": v(2.39, 19.04) * mm, "end": v(1.6, 19.12) * mm});
            skLineSegment(sketch, "E352", {"start": v(1.6, 19.12) * mm, "end": v(1.6, 19.14) * mm});
            skLineSegment(sketch, "E353", {"start": v(1.6, 19.14) * mm, "end": v(1.56, 19.46) * mm});
            skLineSegment(sketch, "E354", {"start": v(1.56, 19.46) * mm, "end": v(1.53, 19.65) * mm});
            skLineSegment(sketch, "E355", {"start": v(1.53, 19.65) * mm, "end": v(1.5, 19.8) * mm});
            skLineSegment(sketch, "E356", {"start": v(1.5, 19.8) * mm, "end": v(1.47, 19.95) * mm});
            skLineSegment(sketch, "E357", {"start": v(1.47, 19.95) * mm, "end": v(1.43, 20.08) * mm});
            skLineSegment(sketch, "E358", {"start": v(1.43, 20.08) * mm, "end": v(1.4, 20.2) * mm});
            skLineSegment(sketch, "E359", {"start": v(1.4, 20.2) * mm, "end": v(1.36, 20.33) * mm});
            skLineSegment(sketch, "E360", {"start": v(1.36, 20.33) * mm, "end": v(1.32, 20.45) * mm});
            skLineSegment(sketch, "E361", {"start": v(1.32, 20.45) * mm, "end": v(1.28, 20.57) * mm});
            skLineSegment(sketch, "E362", {"start": v(1.28, 20.57) * mm, "end": v(1.24, 20.69) * mm});
            skLineSegment(sketch, "E363", {"start": v(1.24, 20.69) * mm, "end": v(1.2, 20.8) * mm});
            skLineSegment(sketch, "E364", {"start": v(1.2, 20.8) * mm, "end": v(1.16, 20.9) * mm});
            skLineSegment(sketch, "E365", {"start": v(1.16, 20.9) * mm, "end": v(1.11, 21.02) * mm});
            skLineSegment(sketch, "E366", {"start": v(1.11, 21.02) * mm, "end": v(1.07, 21.12) * mm});
            skLineSegment(sketch, "E367", {"start": v(1.07, 21.12) * mm, "end": v(0.38, 21.15) * mm});
            skLineSegment(sketch, "E368", {"start": v(0.38, 21.15) * mm, "end": v(0.33, 21.04) * mm});
            skLineSegment(sketch, "E369", {"start": v(0.33, 21.04) * mm, "end": v(0.28, 20.94) * mm});
            skLineSegment(sketch, "E370", {"start": v(0.28, 20.94) * mm, "end": v(0.23, 20.83) * mm});
            skLineSegment(sketch, "E371", {"start": v(0.23, 20.83) * mm, "end": v(0.18, 20.72) * mm});
            skLineSegment(sketch, "E372", {"start": v(0.18, 20.72) * mm, "end": v(0.13, 20.61) * mm});
            skLineSegment(sketch, "E373", {"start": v(0.13, 20.61) * mm, "end": v(0.08, 20.5) * mm});
            skLineSegment(sketch, "E374", {"start": v(0.08, 20.5) * mm, "end": v(0.04, 20.38) * mm});
            skLineSegment(sketch, "E375", {"start": v(0.04, 20.38) * mm, "end": v(-0.01, 20.26) * mm});
            skLineSegment(sketch, "E376", {"start": v(-0.01, 20.26) * mm, "end": v(-0.06, 20.13) * mm});
            skLineSegment(sketch, "E377", {"start": v(-0.06, 20.13) * mm, "end": v(-0.1, 20) * mm});
            skLineSegment(sketch, "E378", {"start": v(-0.1, 20) * mm, "end": v(-0.14, 19.86) * mm});
            skLineSegment(sketch, "E379", {"start": v(-0.14, 19.86) * mm, "end": v(-0.18, 19.7) * mm});
            skLineSegment(sketch, "E380", {"start": v(-0.18, 19.7) * mm, "end": v(-0.23, 19.53) * mm});
            skLineSegment(sketch, "E381", {"start": v(-0.23, 19.53) * mm, "end": v(-0.28, 19.2) * mm});
            skLineSegment(sketch, "E382", {"start": v(-0.28, 19.2) * mm, "end": v(-0.28, 19.19) * mm});
            skLineSegment(sketch, "E383", {"start": v(-0.28, 19.19) * mm, "end": v(-1.08, 19.16) * mm});
            skLineSegment(sketch, "E384", {"start": v(-1.08, 19.16) * mm, "end": v(-1.08, 19.18) * mm});
            skLineSegment(sketch, "E385", {"start": v(-1.08, 19.18) * mm, "end": v(-1.16, 19.5) * mm});
            skLineSegment(sketch, "E386", {"start": v(-1.16, 19.5) * mm, "end": v(-1.22, 19.67) * mm});
            skLineSegment(sketch, "E387", {"start": v(-1.22, 19.67) * mm, "end": v(-1.27, 19.82) * mm});
            skLineSegment(sketch, "E388", {"start": v(-1.27, 19.82) * mm, "end": v(-1.32, 19.96) * mm});
            skLineSegment(sketch, "E389", {"start": v(-1.32, 19.96) * mm, "end": v(-1.38, 20.09) * mm});
            skLineSegment(sketch, "E390", {"start": v(-1.38, 20.09) * mm, "end": v(-1.43, 20.2) * mm});
            skLineSegment(sketch, "E391", {"start": v(-1.43, 20.2) * mm, "end": v(-1.48, 20.33) * mm});
            skLineSegment(sketch, "E392", {"start": v(-1.48, 20.33) * mm, "end": v(-1.54, 20.44) * mm});
            skLineSegment(sketch, "E393", {"start": v(-1.54, 20.44) * mm, "end": v(-1.6, 20.55) * mm});
            skLineSegment(sketch, "E394", {"start": v(-1.6, 20.55) * mm, "end": v(-1.65, 20.66) * mm});
            skLineSegment(sketch, "E395", {"start": v(-1.65, 20.66) * mm, "end": v(-1.7, 20.76) * mm});
            skLineSegment(sketch, "E396", {"start": v(-1.7, 20.76) * mm, "end": v(-1.76, 20.87) * mm});
            skLineSegment(sketch, "E397", {"start": v(-1.76, 20.87) * mm, "end": v(-1.82, 20.97) * mm});
            skLineSegment(sketch, "E398", {"start": v(-1.82, 20.97) * mm, "end": v(-1.88, 21.07) * mm});
            skLineSegment(sketch, "E399", {"start": v(-1.88, 21.07) * mm, "end": v(-2.57, 21) * mm});
            skLineSegment(sketch, "E400", {"start": v(-2.57, 21) * mm, "end": v(-2.6, 20.89) * mm});
            skLineSegment(sketch, "E401", {"start": v(-2.6, 20.89) * mm, "end": v(-2.64, 20.78) * mm});
            skLineSegment(sketch, "E402", {"start": v(-2.64, 20.78) * mm, "end": v(-2.68, 20.66) * mm});
            skLineSegment(sketch, "E403", {"start": v(-2.68, 20.66) * mm, "end": v(-2.7, 20.55) * mm});
            skLineSegment(sketch, "E404", {"start": v(-2.7, 20.55) * mm, "end": v(-2.74, 20.43) * mm});
            skLineSegment(sketch, "E405", {"start": v(-2.74, 20.43) * mm, "end": v(-2.77, 20.31) * mm});
            skLineSegment(sketch, "E406", {"start": v(-2.77, 20.31) * mm, "end": v(-2.8, 20.19) * mm});
            skLineSegment(sketch, "E407", {"start": v(-2.8, 20.19) * mm, "end": v(-2.83, 20.06) * mm});
            skLineSegment(sketch, "E408", {"start": v(-2.83, 20.06) * mm, "end": v(-2.86, 19.93) * mm});
            skLineSegment(sketch, "E409", {"start": v(-2.86, 19.93) * mm, "end": v(-2.88, 19.8) * mm});
            skLineSegment(sketch, "E410", {"start": v(-2.88, 19.8) * mm, "end": v(-2.9, 19.65) * mm});
            skLineSegment(sketch, "E411", {"start": v(-2.9, 19.65) * mm, "end": v(-2.93, 19.49) * mm});
            skLineSegment(sketch, "E412", {"start": v(-2.93, 19.49) * mm, "end": v(-2.94, 19.3) * mm});
            skLineSegment(sketch, "E413", {"start": v(-2.94, 19.3) * mm, "end": v(-2.95, 18.98) * mm});
            skLineSegment(sketch, "E414", {"start": v(-2.95, 18.98) * mm, "end": v(-2.95, 18.96) * mm});
            skLineSegment(sketch, "E415", {"start": v(-2.95, 18.96) * mm, "end": v(-3.74, 18.82) * mm});
            skLineSegment(sketch, "E416", {"start": v(-3.74, 18.82) * mm, "end": v(-3.74, 18.84) * mm});
            skLineSegment(sketch, "E417", {"start": v(-3.74, 18.84) * mm, "end": v(-3.86, 19.15) * mm});
            skLineSegment(sketch, "E418", {"start": v(-3.86, 19.15) * mm, "end": v(-3.94, 19.31) * mm});
            skLineSegment(sketch, "E419", {"start": v(-3.94, 19.31) * mm, "end": v(-4.02, 19.45) * mm});
            skLineSegment(sketch, "E420", {"start": v(-4.02, 19.45) * mm, "end": v(-4.09, 19.58) * mm});
            skLineSegment(sketch, "E421", {"start": v(-4.09, 19.58) * mm, "end": v(-4.16, 19.7) * mm});
            skLineSegment(sketch, "E422", {"start": v(-4.16, 19.7) * mm, "end": v(-4.23, 19.82) * mm});
            skLineSegment(sketch, "E423", {"start": v(-4.23, 19.82) * mm, "end": v(-4.3, 19.92) * mm});
            skLineSegment(sketch, "E424", {"start": v(-4.3, 19.92) * mm, "end": v(-4.37, 20.03) * mm});
            skLineSegment(sketch, "E425", {"start": v(-4.37, 20.03) * mm, "end": v(-4.44, 20.13) * mm});
            skLineSegment(sketch, "E426", {"start": v(-4.44, 20.13) * mm, "end": v(-4.5, 20.23) * mm});
            skLineSegment(sketch, "E427", {"start": v(-4.5, 20.23) * mm, "end": v(-4.58, 20.33) * mm});
            skLineSegment(sketch, "E428", {"start": v(-4.58, 20.33) * mm, "end": v(-4.65, 20.42) * mm});
            skLineSegment(sketch, "E429", {"start": v(-4.65, 20.42) * mm, "end": v(-4.72, 20.51) * mm});
            skLineSegment(sketch, "E430", {"start": v(-4.72, 20.51) * mm, "end": v(-4.8, 20.6) * mm});
            skLineSegment(sketch, "E431", {"start": v(-4.8, 20.6) * mm, "end": v(-5.47, 20.44) * mm});
            skLineSegment(sketch, "E432", {"start": v(-5.47, 20.44) * mm, "end": v(-5.49, 20.32) * mm});
            skLineSegment(sketch, "E433", {"start": v(-5.49, 20.32) * mm, "end": v(-5.5, 20.2) * mm});
            skLineSegment(sketch, "E434", {"start": v(-5.5, 20.2) * mm, "end": v(-5.52, 20.1) * mm});
            skLineSegment(sketch, "E435", {"start": v(-5.52, 20.1) * mm, "end": v(-5.54, 19.97) * mm});
            skLineSegment(sketch, "E436", {"start": v(-5.54, 19.97) * mm, "end": v(-5.56, 19.85) * mm});
            skLineSegment(sketch, "E437", {"start": v(-5.56, 19.85) * mm, "end": v(-5.57, 19.73) * mm});
            skLineSegment(sketch, "E438", {"start": v(-5.57, 19.73) * mm, "end": v(-5.58, 19.6) * mm});
            skLineSegment(sketch, "E439", {"start": v(-5.58, 19.6) * mm, "end": v(-5.6, 19.47) * mm});
            skLineSegment(sketch, "E440", {"start": v(-5.6, 19.47) * mm, "end": v(-5.6, 19.34) * mm});
            skLineSegment(sketch, "E441", {"start": v(-5.6, 19.34) * mm, "end": v(-5.6, 19.2) * mm});
            skLineSegment(sketch, "E442", {"start": v(-5.6, 19.2) * mm, "end": v(-5.61, 19.05) * mm});
            skLineSegment(sketch, "E443", {"start": v(-5.61, 19.05) * mm, "end": v(-5.6, 18.9) * mm});
            skLineSegment(sketch, "E444", {"start": v(-5.6, 18.9) * mm, "end": v(-5.6, 18.71) * mm});
            skLineSegment(sketch, "E445", {"start": v(-5.6, 18.71) * mm, "end": v(-5.57, 18.39) * mm});
            skLineSegment(sketch, "E446", {"start": v(-5.57, 18.39) * mm, "end": v(-5.56, 18.37) * mm});
            skLineSegment(sketch, "E447", {"start": v(-5.56, 18.37) * mm, "end": v(-6.32, 18.12) * mm});
            skLineSegment(sketch, "E448", {"start": v(-6.32, 18.12) * mm, "end": v(-6.33, 18.14) * mm});
            skLineSegment(sketch, "E449", {"start": v(-6.33, 18.14) * mm, "end": v(-6.5, 18.42) * mm});
            skLineSegment(sketch, "E450", {"start": v(-6.5, 18.42) * mm, "end": v(-6.6, 18.58) * mm});
            skLineSegment(sketch, "E451", {"start": v(-6.6, 18.58) * mm, "end": v(-6.69, 18.7) * mm});
            skLineSegment(sketch, "E452", {"start": v(-6.69, 18.7) * mm, "end": v(-6.77, 18.82) * mm});
            skLineSegment(sketch, "E453", {"start": v(-6.77, 18.82) * mm, "end": v(-6.86, 18.93) * mm});
            skLineSegment(sketch, "E454", {"start": v(-6.86, 18.93) * mm, "end": v(-6.95, 19.04) * mm});
            skLineSegment(sketch, "E455", {"start": v(-6.95, 19.04) * mm, "end": v(-7.03, 19.13) * mm});
            skLineSegment(sketch, "E456", {"start": v(-7.03, 19.13) * mm, "end": v(-7.11, 19.23) * mm});
            skLineSegment(sketch, "E457", {"start": v(-7.11, 19.23) * mm, "end": v(-7.2, 19.32) * mm});
            skLineSegment(sketch, "E458", {"start": v(-7.2, 19.32) * mm, "end": v(-7.28, 19.4) * mm});
            skLineSegment(sketch, "E459", {"start": v(-7.28, 19.4) * mm, "end": v(-7.36, 19.5) * mm});
            skLineSegment(sketch, "E460", {"start": v(-7.36, 19.5) * mm, "end": v(-7.45, 19.58) * mm});
            skLineSegment(sketch, "E461", {"start": v(-7.45, 19.58) * mm, "end": v(-7.53, 19.66) * mm});
            skLineSegment(sketch, "E462", {"start": v(-7.53, 19.66) * mm, "end": v(-7.62, 19.74) * mm});
            skLineSegment(sketch, "E463", {"start": v(-7.62, 19.74) * mm, "end": v(-8.26, 19.48) * mm});
            skLineSegment(sketch, "E464", {"start": v(-8.26, 19.48) * mm, "end": v(-8.26, 19.36) * mm});
            skLineSegment(sketch, "E465", {"start": v(-8.26, 19.36) * mm, "end": v(-8.27, 19.25) * mm});
            skLineSegment(sketch, "E466", {"start": v(-8.27, 19.25) * mm, "end": v(-8.27, 19.13) * mm});
            skLineSegment(sketch, "E467", {"start": v(-8.27, 19.13) * mm, "end": v(-8.27, 19) * mm});
            skLineSegment(sketch, "E468", {"start": v(-8.27, 19) * mm, "end": v(-8.27, 18.89) * mm});
            skLineSegment(sketch, "E469", {"start": v(-8.27, 18.89) * mm, "end": v(-8.26, 18.76) * mm});
            skLineSegment(sketch, "E470", {"start": v(-8.26, 18.76) * mm, "end": v(-8.26, 18.64) * mm});
            skLineSegment(sketch, "E471", {"start": v(-8.26, 18.64) * mm, "end": v(-8.25, 18.5) * mm});
            skLineSegment(sketch, "E472", {"start": v(-8.25, 18.5) * mm, "end": v(-8.24, 18.37) * mm});
            skLineSegment(sketch, "E473", {"start": v(-8.24, 18.37) * mm, "end": v(-8.23, 18.24) * mm});
            skLineSegment(sketch, "E474", {"start": v(-8.23, 18.24) * mm, "end": v(-8.2, 18.09) * mm});
            skLineSegment(sketch, "E475", {"start": v(-8.2, 18.09) * mm, "end": v(-8.18, 17.93) * mm});
            skLineSegment(sketch, "E476", {"start": v(-8.18, 17.93) * mm, "end": v(-8.15, 17.75) * mm});
            skLineSegment(sketch, "E477", {"start": v(-8.15, 17.75) * mm, "end": v(-8.07, 17.44) * mm});
            skLineSegment(sketch, "E478", {"start": v(-8.07, 17.44) * mm, "end": v(-8.06, 17.42) * mm});
            skLineSegment(sketch, "E479", {"start": v(-8.06, 17.42) * mm, "end": v(-8.78, 17.07) * mm});
            skLineSegment(sketch, "E480", {"start": v(-8.78, 17.07) * mm, "end": v(-8.8, 17.09) * mm});
            skLineSegment(sketch, "E481", {"start": v(-8.8, 17.09) * mm, "end": v(-9, 17.34) * mm});
            skLineSegment(sketch, "E482", {"start": v(-9, 17.34) * mm, "end": v(-9.11, 17.48) * mm});
            skLineSegment(sketch, "E483", {"start": v(-9.11, 17.48) * mm, "end": v(-9.22, 17.6) * mm});
            skLineSegment(sketch, "E484", {"start": v(-9.22, 17.6) * mm, "end": v(-9.33, 17.7) * mm});
            skLineSegment(sketch, "E485", {"start": v(-9.33, 17.7) * mm, "end": v(-9.43, 17.8) * mm});
            skLineSegment(sketch, "E486", {"start": v(-9.43, 17.8) * mm, "end": v(-9.53, 17.89) * mm});
            skLineSegment(sketch, "E487", {"start": v(-9.53, 17.89) * mm, "end": v(-9.62, 17.97) * mm});
            skLineSegment(sketch, "E488", {"start": v(-9.62, 17.97) * mm, "end": v(-9.72, 18.05) * mm});
            skLineSegment(sketch, "E489", {"start": v(-9.72, 18.05) * mm, "end": v(-9.82, 18.13) * mm});
            skLineSegment(sketch, "E490", {"start": v(-9.82, 18.13) * mm, "end": v(-9.91, 18.2) * mm});
            skLineSegment(sketch, "E491", {"start": v(-9.91, 18.2) * mm, "end": v(-10, 18.28) * mm});
            skLineSegment(sketch, "E492", {"start": v(-10, 18.28) * mm, "end": v(-10.1, 18.35) * mm});
            skLineSegment(sketch, "E493", {"start": v(-10.1, 18.35) * mm, "end": v(-10.2, 18.42) * mm});
            skLineSegment(sketch, "E494", {"start": v(-10.2, 18.42) * mm, "end": v(-10.29, 18.49) * mm});
            skLineSegment(sketch, "E495", {"start": v(-10.29, 18.49) * mm, "end": v(-10.89, 18.14) * mm});
            skLineSegment(sketch, "E496", {"start": v(-10.89, 18.14) * mm, "end": v(-10.88, 18.03) * mm});
            skLineSegment(sketch, "E497", {"start": v(-10.88, 18.03) * mm, "end": v(-10.86, 17.91) * mm});
            skLineSegment(sketch, "E498", {"start": v(-10.86, 17.91) * mm, "end": v(-10.85, 17.8) * mm});
            skLineSegment(sketch, "E499", {"start": v(-10.85, 17.8) * mm, "end": v(-10.83, 17.68) * mm});
            skLineSegment(sketch, "E500", {"start": v(-10.83, 17.68) * mm, "end": v(-10.82, 17.56) * mm});
            skLineSegment(sketch, "E501", {"start": v(-10.82, 17.56) * mm, "end": v(-10.8, 17.43) * mm});
            skLineSegment(sketch, "E502", {"start": v(-10.8, 17.43) * mm, "end": v(-10.77, 17.3) * mm});
            skLineSegment(sketch, "E503", {"start": v(-10.77, 17.3) * mm, "end": v(-10.75, 17.18) * mm});
            skLineSegment(sketch, "E504", {"start": v(-10.75, 17.18) * mm, "end": v(-10.72, 17.05) * mm});
            skLineSegment(sketch, "E505", {"start": v(-10.72, 17.05) * mm, "end": v(-10.68, 16.92) * mm});
            skLineSegment(sketch, "E506", {"start": v(-10.68, 16.92) * mm, "end": v(-10.65, 16.77) * mm});
            skLineSegment(sketch, "E507", {"start": v(-10.65, 16.77) * mm, "end": v(-10.6, 16.62) * mm});
            skLineSegment(sketch, "E508", {"start": v(-10.6, 16.62) * mm, "end": v(-10.54, 16.45) * mm});
            skLineSegment(sketch, "E509", {"start": v(-10.54, 16.45) * mm, "end": v(-10.42, 16.15) * mm});
            skLineSegment(sketch, "E510", {"start": v(-10.42, 16.15) * mm, "end": v(-10.41, 16.13) * mm});
            skLineSegment(sketch, "E511", {"start": v(-10.41, 16.13) * mm, "end": v(-11.07, 15.68) * mm});
            skLineSegment(sketch, "E512", {"start": v(-11.07, 15.68) * mm, "end": v(-11.09, 15.7) * mm});
            skLineSegment(sketch, "E513", {"start": v(-11.09, 15.7) * mm, "end": v(-11.32, 15.92) * mm});
            skLineSegment(sketch, "E514", {"start": v(-11.32, 15.92) * mm, "end": v(-11.46, 16.04) * mm});
            skLineSegment(sketch, "E515", {"start": v(-11.46, 16.04) * mm, "end": v(-11.58, 16.14) * mm});
            skLineSegment(sketch, "E516", {"start": v(-11.58, 16.14) * mm, "end": v(-11.7, 16.23) * mm});
            skLineSegment(sketch, "E517", {"start": v(-11.7, 16.23) * mm, "end": v(-11.81, 16.31) * mm});
            skLineSegment(sketch, "E518", {"start": v(-11.81, 16.31) * mm, "end": v(-11.92, 16.39) * mm});
            skLineSegment(sketch, "E519", {"start": v(-11.92, 16.39) * mm, "end": v(-12.03, 16.46) * mm});
            skLineSegment(sketch, "E520", {"start": v(-12.03, 16.46) * mm, "end": v(-12.14, 16.53) * mm});
            skLineSegment(sketch, "E521", {"start": v(-12.14, 16.53) * mm, "end": v(-12.24, 16.6) * mm});
            skLineSegment(sketch, "E522", {"start": v(-12.24, 16.6) * mm, "end": v(-12.35, 16.65) * mm});
            skLineSegment(sketch, "E523", {"start": v(-12.35, 16.65) * mm, "end": v(-12.45, 16.71) * mm});
            skLineSegment(sketch, "E524", {"start": v(-12.45, 16.71) * mm, "end": v(-12.56, 16.77) * mm});
            skLineSegment(sketch, "E525", {"start": v(-12.56, 16.77) * mm, "end": v(-12.66, 16.82) * mm});
            skLineSegment(sketch, "E526", {"start": v(-12.66, 16.82) * mm, "end": v(-12.76, 16.88) * mm});
            skLineSegment(sketch, "E527", {"start": v(-12.76, 16.88) * mm, "end": v(-13.3, 16.45) * mm});
            skLineSegment(sketch, "E528", {"start": v(-13.3, 16.45) * mm, "end": v(-13.28, 16.34) * mm});
            skLineSegment(sketch, "E529", {"start": v(-13.28, 16.34) * mm, "end": v(-13.25, 16.23) * mm});
            skLineSegment(sketch, "E530", {"start": v(-13.25, 16.23) * mm, "end": v(-13.22, 16.11) * mm});
            skLineSegment(sketch, "E531", {"start": v(-13.22, 16.11) * mm, "end": v(-13.19, 16) * mm});
            skLineSegment(sketch, "E532", {"start": v(-13.19, 16) * mm, "end": v(-13.15, 15.88) * mm});
            skLineSegment(sketch, "E533", {"start": v(-13.15, 15.88) * mm, "end": v(-13.12, 15.76) * mm});
            skLineSegment(sketch, "E534", {"start": v(-13.12, 15.76) * mm, "end": v(-13.08, 15.64) * mm});
            skLineSegment(sketch, "E535", {"start": v(-13.08, 15.64) * mm, "end": v(-13.03, 15.52) * mm});
            skLineSegment(sketch, "E536", {"start": v(-13.03, 15.52) * mm, "end": v(-12.99, 15.4) * mm});
            skLineSegment(sketch, "E537", {"start": v(-12.99, 15.4) * mm, "end": v(-12.93, 15.27) * mm});
            skLineSegment(sketch, "E538", {"start": v(-12.93, 15.27) * mm, "end": v(-12.88, 15.13) * mm});
            skLineSegment(sketch, "E539", {"start": v(-12.88, 15.13) * mm, "end": v(-12.81, 14.99) * mm});
            skLineSegment(sketch, "E540", {"start": v(-12.81, 14.99) * mm, "end": v(-12.73, 14.82) * mm});
            skLineSegment(sketch, "E541", {"start": v(-12.73, 14.82) * mm, "end": v(-12.57, 14.54) * mm});
            skLineSegment(sketch, "E542", {"start": v(-12.57, 14.54) * mm, "end": v(-12.55, 14.53) * mm});
            skLineSegment(sketch, "E543", {"start": v(-12.55, 14.53) * mm, "end": v(-13.15, 13.99) * mm});
            skLineSegment(sketch, "E544", {"start": v(-13.15, 13.99) * mm, "end": v(-13.16, 14) * mm});
            skLineSegment(sketch, "E545", {"start": v(-13.16, 14) * mm, "end": v(-13.42, 14.2) * mm});
            skLineSegment(sketch, "E546", {"start": v(-13.42, 14.2) * mm, "end": v(-13.58, 14.3) * mm});
            skLineSegment(sketch, "E547", {"start": v(-13.58, 14.3) * mm, "end": v(-13.72, 14.37) * mm});
            skLineSegment(sketch, "E548", {"start": v(-13.72, 14.37) * mm, "end": v(-13.85, 14.45) * mm});
            skLineSegment(sketch, "E549", {"start": v(-13.85, 14.45) * mm, "end": v(-13.97, 14.51) * mm});
            skLineSegment(sketch, "E550", {"start": v(-13.97, 14.51) * mm, "end": v(-14.09, 14.57) * mm});
            skLineSegment(sketch, "E551", {"start": v(-14.09, 14.57) * mm, "end": v(-14.2, 14.63) * mm});
            skLineSegment(sketch, "E552", {"start": v(-14.2, 14.63) * mm, "end": v(-14.32, 14.68) * mm});
            skLineSegment(sketch, "E553", {"start": v(-14.32, 14.68) * mm, "end": v(-14.43, 14.73) * mm});
            skLineSegment(sketch, "E554", {"start": v(-14.43, 14.73) * mm, "end": v(-14.55, 14.77) * mm});
            skLineSegment(sketch, "E555", {"start": v(-14.55, 14.77) * mm, "end": v(-14.66, 14.82) * mm});
            skLineSegment(sketch, "E556", {"start": v(-14.66, 14.82) * mm, "end": v(-14.77, 14.86) * mm});
            skLineSegment(sketch, "E557", {"start": v(-14.77, 14.86) * mm, "end": v(-14.88, 14.9) * mm});
            skLineSegment(sketch, "E558", {"start": v(-14.88, 14.9) * mm, "end": v(-14.99, 14.94) * mm});
            skLineSegment(sketch, "E559", {"start": v(-14.99, 14.94) * mm, "end": v(-15.47, 14.44) * mm});
            skLineSegment(sketch, "E560", {"start": v(-15.47, 14.44) * mm, "end": v(-15.42, 14.33) * mm});
            skLineSegment(sketch, "E561", {"start": v(-15.42, 14.33) * mm, "end": v(-15.38, 14.23) * mm});
            skLineSegment(sketch, "E562", {"start": v(-15.38, 14.23) * mm, "end": v(-15.33, 14.12) * mm});
            skLineSegment(sketch, "E563", {"start": v(-15.33, 14.12) * mm, "end": v(-15.29, 14) * mm});
            skLineSegment(sketch, "E564", {"start": v(-15.29, 14) * mm, "end": v(-15.24, 13.9) * mm});
            skLineSegment(sketch, "E565", {"start": v(-15.24, 13.9) * mm, "end": v(-15.18, 13.79) * mm});
            skLineSegment(sketch, "E566", {"start": v(-15.18, 13.79) * mm, "end": v(-15.13, 13.67) * mm});
            skLineSegment(sketch, "E567", {"start": v(-15.13, 13.67) * mm, "end": v(-15.07, 13.56) * mm});
            skLineSegment(sketch, "E568", {"start": v(-15.07, 13.56) * mm, "end": v(-15, 13.44) * mm});
            skLineSegment(sketch, "E569", {"start": v(-15, 13.44) * mm, "end": v(-14.93, 13.32) * mm});
            skLineSegment(sketch, "E570", {"start": v(-14.93, 13.32) * mm, "end": v(-14.86, 13.2) * mm});
            skLineSegment(sketch, "E571", {"start": v(-14.86, 13.2) * mm, "end": v(-14.77, 13.06) * mm});
            skLineSegment(sketch, "E572", {"start": v(-14.77, 13.06) * mm, "end": v(-14.67, 12.9) * mm});
            skLineSegment(sketch, "E573", {"start": v(-14.67, 12.9) * mm, "end": v(-14.47, 12.65) * mm});
            skLineSegment(sketch, "E574", {"start": v(-14.47, 12.65) * mm, "end": v(-14.45, 12.64) * mm});
            skLineSegment(sketch, "E575", {"start": v(-14.45, 12.64) * mm, "end": v(-14.97, 12.03) * mm});
            skLineSegment(sketch, "E576", {"start": v(-14.97, 12.03) * mm, "end": v(-14.98, 12.04) * mm});
            skLineSegment(sketch, "E577", {"start": v(-14.98, 12.04) * mm, "end": v(-15.27, 12.2) * mm});
            skLineSegment(sketch, "E578", {"start": v(-15.27, 12.2) * mm, "end": v(-15.44, 12.27) * mm});
            skLineSegment(sketch, "E579", {"start": v(-15.44, 12.27) * mm, "end": v(-15.58, 12.33) * mm});
            skLineSegment(sketch, "E580", {"start": v(-15.58, 12.33) * mm, "end": v(-15.72, 12.38) * mm});
            skLineSegment(sketch, "E581", {"start": v(-15.72, 12.38) * mm, "end": v(-15.85, 12.43) * mm});
            skLineSegment(sketch, "E582", {"start": v(-15.85, 12.43) * mm, "end": v(-15.98, 12.47) * mm});
            skLineSegment(sketch, "E583", {"start": v(-15.98, 12.47) * mm, "end": v(-16.1, 12.5) * mm});
            skLineSegment(sketch, "E584", {"start": v(-16.1, 12.5) * mm, "end": v(-16.22, 12.54) * mm});
            skLineSegment(sketch, "E585", {"start": v(-16.22, 12.54) * mm, "end": v(-16.34, 12.58) * mm});
            skLineSegment(sketch, "E586", {"start": v(-16.34, 12.58) * mm, "end": v(-16.46, 12.6) * mm});
            skLineSegment(sketch, "E587", {"start": v(-16.46, 12.6) * mm, "end": v(-16.58, 12.64) * mm});
            skLineSegment(sketch, "E588", {"start": v(-16.58, 12.64) * mm, "end": v(-16.7, 12.66) * mm});
            skLineSegment(sketch, "E589", {"start": v(-16.7, 12.66) * mm, "end": v(-16.8, 12.69) * mm});
            skLineSegment(sketch, "E590", {"start": v(-16.8, 12.69) * mm, "end": v(-16.92, 12.7) * mm});
            skLineSegment(sketch, "E591", {"start": v(-16.92, 12.7) * mm, "end": v(-17.33, 12.15) * mm});
            skLineSegment(sketch, "E592", {"start": v(-17.33, 12.15) * mm, "end": v(-17.27, 12.05) * mm});
            skLineSegment(sketch, "E593", {"start": v(-17.27, 12.05) * mm, "end": v(-17.21, 11.95) * mm});
            skLineSegment(sketch, "E594", {"start": v(-17.21, 11.95) * mm, "end": v(-17.15, 11.85) * mm});
            skLineSegment(sketch, "E595", {"start": v(-17.15, 11.85) * mm, "end": v(-17.09, 11.75) * mm});
            skLineSegment(sketch, "E596", {"start": v(-17.09, 11.75) * mm, "end": v(-17.02, 11.64) * mm});
            skLineSegment(sketch, "E597", {"start": v(-17.02, 11.64) * mm, "end": v(-16.95, 11.54) * mm});
            skLineSegment(sketch, "E598", {"start": v(-16.95, 11.54) * mm, "end": v(-16.88, 11.44) * mm});
            skLineSegment(sketch, "E599", {"start": v(-16.88, 11.44) * mm, "end": v(-16.8, 11.33) * mm});
            skLineSegment(sketch, "E600", {"start": v(-16.8, 11.33) * mm, "end": v(-16.73, 11.22) * mm});
            skLineSegment(sketch, "E601", {"start": v(-16.73, 11.22) * mm, "end": v(-16.64, 11.11) * mm});
            skLineSegment(sketch, "E602", {"start": v(-16.64, 11.11) * mm, "end": v(-16.55, 11) * mm});
            skLineSegment(sketch, "E603", {"start": v(-16.55, 11) * mm, "end": v(-16.45, 10.88) * mm});
            skLineSegment(sketch, "E604", {"start": v(-16.45, 10.88) * mm, "end": v(-16.32, 10.74) * mm});
            skLineSegment(sketch, "E605", {"start": v(-16.32, 10.74) * mm, "end": v(-16.09, 10.52) * mm});
            skLineSegment(sketch, "E606", {"start": v(-16.09, 10.52) * mm, "end": v(-16.07, 10.5) * mm});
            skLineSegment(sketch, "E607", {"start": v(-16.07, 10.5) * mm, "end": v(-16.5, 9.83) * mm});
            skLineSegment(sketch, "E608", {"start": v(-16.5, 9.83) * mm, "end": v(-16.51, 9.84) * mm});
            skLineSegment(sketch, "E609", {"start": v(-16.51, 9.84) * mm, "end": v(-16.82, 9.95) * mm});
            skLineSegment(sketch, "E610", {"start": v(-16.82, 9.95) * mm, "end": v(-17, 10) * mm});
            skLineSegment(sketch, "E611", {"start": v(-17, 10) * mm, "end": v(-17.15, 10.04) * mm});
            skLineSegment(sketch, "E612", {"start": v(-17.15, 10.04) * mm, "end": v(-17.3, 10.07) * mm});
            skLineSegment(sketch, "E613", {"start": v(-17.3, 10.07) * mm, "end": v(-17.43, 10.1) * mm});
            skLineSegment(sketch, "E614", {"start": v(-17.43, 10.1) * mm, "end": v(-17.56, 10.13) * mm});
            skLineSegment(sketch, "E615", {"start": v(-17.56, 10.13) * mm, "end": v(-17.69, 10.15) * mm});
            skLineSegment(sketch, "E616", {"start": v(-17.69, 10.15) * mm, "end": v(-17.81, 10.17) * mm});
            skLineSegment(sketch, "E617", {"start": v(-17.81, 10.17) * mm, "end": v(-17.94, 10.18) * mm});
            skLineSegment(sketch, "E618", {"start": v(-17.94, 10.18) * mm, "end": v(-18.06, 10.2) * mm});
            skLineSegment(sketch, "E619", {"start": v(-18.06, 10.2) * mm, "end": v(-18.18, 10.2) * mm});
            skLineSegment(sketch, "E620", {"start": v(-18.18, 10.2) * mm, "end": v(-18.3, 10.22) * mm});
            skLineSegment(sketch, "E621", {"start": v(-18.3, 10.22) * mm, "end": v(-18.4, 10.23) * mm});
            skLineSegment(sketch, "E622", {"start": v(-18.4, 10.23) * mm, "end": v(-18.52, 10.23) * mm});
            skLineSegment(sketch, "E623", {"start": v(-18.52, 10.23) * mm, "end": v(-18.85, 9.62) * mm});
            skLineSegment(sketch, "E624", {"start": v(-18.85, 9.62) * mm, "end": v(-18.78, 9.53) * mm});
            skLineSegment(sketch, "E625", {"start": v(-18.78, 9.53) * mm, "end": v(-18.7, 9.44) * mm});
            skLineSegment(sketch, "E626", {"start": v(-18.7, 9.44) * mm, "end": v(-18.63, 9.35) * mm});
            skLineSegment(sketch, "E627", {"start": v(-18.63, 9.35) * mm, "end": v(-18.56, 9.26) * mm});
            skLineSegment(sketch, "E628", {"start": v(-18.56, 9.26) * mm, "end": v(-18.48, 9.16) * mm});
            skLineSegment(sketch, "E629", {"start": v(-18.48, 9.16) * mm, "end": v(-18.4, 9.07) * mm});
            skLineSegment(sketch, "E630", {"start": v(-18.4, 9.07) * mm, "end": v(-18.3, 8.98) * mm});
            skLineSegment(sketch, "E631", {"start": v(-18.3, 8.98) * mm, "end": v(-18.22, 8.88) * mm});
            skLineSegment(sketch, "E632", {"start": v(-18.22, 8.88) * mm, "end": v(-18.13, 8.79) * mm});
            skLineSegment(sketch, "E633", {"start": v(-18.13, 8.79) * mm, "end": v(-18.03, 8.7) * mm});
            skLineSegment(sketch, "E634", {"start": v(-18.03, 8.7) * mm, "end": v(-17.92, 8.6) * mm});
            skLineSegment(sketch, "E635", {"start": v(-17.92, 8.6) * mm, "end": v(-17.8, 8.48) * mm});
            skLineSegment(sketch, "E636", {"start": v(-17.8, 8.48) * mm, "end": v(-17.66, 8.37) * mm});
            skLineSegment(sketch, "E637", {"start": v(-17.66, 8.37) * mm, "end": v(-17.4, 8.18) * mm});
            skLineSegment(sketch, "E638", {"start": v(-17.4, 8.18) * mm, "end": v(-17.38, 8.17) * mm});
            skLineSegment(sketch, "E639", {"start": v(-17.38, 8.17) * mm, "end": v(-17.7, 7.44) * mm});
            skLineSegment(sketch, "E640", {"start": v(-17.7, 7.44) * mm, "end": v(-17.72, 7.45) * mm});
            skLineSegment(sketch, "E641", {"start": v(-17.72, 7.45) * mm, "end": v(-18.04, 7.51) * mm});
            skLineSegment(sketch, "E642", {"start": v(-18.04, 7.51) * mm, "end": v(-18.22, 7.54) * mm});
            skLineSegment(sketch, "E643", {"start": v(-18.22, 7.54) * mm, "end": v(-18.38, 7.56) * mm});
            skLineSegment(sketch, "E644", {"start": v(-18.38, 7.56) * mm, "end": v(-18.53, 7.57) * mm});
            skLineSegment(sketch, "E645", {"start": v(-18.53, 7.57) * mm, "end": v(-18.66, 7.58) * mm});
            skLineSegment(sketch, "E646", {"start": v(-18.66, 7.58) * mm, "end": v(-18.8, 7.59) * mm});
            skLineSegment(sketch, "E647", {"start": v(-18.8, 7.59) * mm, "end": v(-18.93, 7.59) * mm});
            skLineSegment(sketch, "E648", {"start": v(-18.93, 7.59) * mm, "end": v(-19.05, 7.6) * mm});
            skLineSegment(sketch, "E649", {"start": v(-19.05, 7.6) * mm, "end": v(-19.18, 7.59) * mm});
            skLineSegment(sketch, "E650", {"start": v(-19.18, 7.59) * mm, "end": v(-19.3, 7.59) * mm});
            skLineSegment(sketch, "E651", {"start": v(-19.3, 7.59) * mm, "end": v(-19.42, 7.58) * mm});
            skLineSegment(sketch, "E652", {"start": v(-19.42, 7.58) * mm, "end": v(-19.54, 7.57) * mm});
            skLineSegment(sketch, "E653", {"start": v(-19.54, 7.57) * mm, "end": v(-19.65, 7.57) * mm});
            skLineSegment(sketch, "E654", {"start": v(-19.65, 7.57) * mm, "end": v(-19.77, 7.56) * mm});
            skLineSegment(sketch, "E655", {"start": v(-19.77, 7.56) * mm, "end": v(-20, 6.9) * mm});
            skLineSegment(sketch, "E656", {"start": v(-20, 6.9) * mm, "end": v(-19.92, 6.83) * mm});
            skLineSegment(sketch, "E657", {"start": v(-19.92, 6.83) * mm, "end": v(-19.84, 6.75) * mm});
            skLineSegment(sketch, "E658", {"start": v(-19.84, 6.75) * mm, "end": v(-19.75, 6.67) * mm});
            skLineSegment(sketch, "E659", {"start": v(-19.75, 6.67) * mm, "end": v(-19.66, 6.59) * mm});
            skLineSegment(sketch, "E660", {"start": v(-19.66, 6.59) * mm, "end": v(-19.57, 6.5) * mm});
            skLineSegment(sketch, "E661", {"start": v(-19.57, 6.5) * mm, "end": v(-19.48, 6.42) * mm});
            skLineSegment(sketch, "E662", {"start": v(-19.48, 6.42) * mm, "end": v(-19.38, 6.34) * mm});
            skLineSegment(sketch, "E663", {"start": v(-19.38, 6.34) * mm, "end": v(-19.28, 6.26) * mm});
            skLineSegment(sketch, "E664", {"start": v(-19.28, 6.26) * mm, "end": v(-19.17, 6.18) * mm});
            skLineSegment(sketch, "E665", {"start": v(-19.17, 6.18) * mm, "end": v(-19.06, 6.1) * mm});
            skLineSegment(sketch, "E666", {"start": v(-19.06, 6.1) * mm, "end": v(-18.94, 6.01) * mm});
            skLineSegment(sketch, "E667", {"start": v(-18.94, 6.01) * mm, "end": v(-18.8, 5.93) * mm});
            skLineSegment(sketch, "E668", {"start": v(-18.8, 5.93) * mm, "end": v(-18.65, 5.83) * mm});
            skLineSegment(sketch, "E669", {"start": v(-18.65, 5.83) * mm, "end": v(-18.36, 5.68) * mm});
            skLineSegment(sketch, "E670", {"start": v(-18.36, 5.68) * mm, "end": v(-18.35, 5.67) * mm});
            skLineSegment(sketch, "E671", {"start": v(-18.35, 5.67) * mm, "end": v(-18.57, 4.9) * mm});
            skLineSegment(sketch, "E672", {"start": v(-18.57, 4.9) * mm, "end": v(-18.58, 4.9) * mm});
            skLineSegment(sketch, "E673", {"start": v(-18.58, 4.9) * mm, "end": v(-18.9, 4.93) * mm});
            skLineSegment(sketch, "E674", {"start": v(-18.9, 4.93) * mm, "end": v(-19.1, 4.93) * mm});
            skLineSegment(sketch, "E675", {"start": v(-19.1, 4.93) * mm, "end": v(-19.25, 4.93) * mm});
            skLineSegment(sketch, "E676", {"start": v(-19.25, 4.93) * mm, "end": v(-19.4, 4.92) * mm});
            skLineSegment(sketch, "E677", {"start": v(-19.4, 4.92) * mm, "end": v(-19.54, 4.91) * mm});
            skLineSegment(sketch, "E678", {"start": v(-19.54, 4.91) * mm, "end": v(-19.67, 4.9) * mm});
            skLineSegment(sketch, "E679", {"start": v(-19.67, 4.9) * mm, "end": v(-19.8, 4.88) * mm});
            skLineSegment(sketch, "E680", {"start": v(-19.8, 4.88) * mm, "end": v(-19.93, 4.87) * mm});
            skLineSegment(sketch, "E681", {"start": v(-19.93, 4.87) * mm, "end": v(-20.05, 4.85) * mm});
            skLineSegment(sketch, "E682", {"start": v(-20.05, 4.85) * mm, "end": v(-20.17, 4.83) * mm});
            skLineSegment(sketch, "E683", {"start": v(-20.17, 4.83) * mm, "end": v(-20.29, 4.8) * mm});
            skLineSegment(sketch, "E684", {"start": v(-20.29, 4.8) * mm, "end": v(-20.4, 4.78) * mm});
            skLineSegment(sketch, "E685", {"start": v(-20.4, 4.78) * mm, "end": v(-20.51, 4.76) * mm});
            skLineSegment(sketch, "E686", {"start": v(-20.51, 4.76) * mm, "end": v(-20.63, 4.74) * mm});
            skLineSegment(sketch, "E687", {"start": v(-20.63, 4.74) * mm, "end": v(-20.77, 4.06) * mm});
            skLineSegment(sketch, "E688", {"start": v(-20.77, 4.06) * mm, "end": v(-20.68, 4) * mm});
            skLineSegment(sketch, "E689", {"start": v(-20.68, 4) * mm, "end": v(-20.58, 3.92) * mm});
            skLineSegment(sketch, "E690", {"start": v(-20.58, 3.92) * mm, "end": v(-20.49, 3.85) * mm});
            skLineSegment(sketch, "E691", {"start": v(-20.49, 3.85) * mm, "end": v(-20.39, 3.79) * mm});
            skLineSegment(sketch, "E692", {"start": v(-20.39, 3.79) * mm, "end": v(-20.29, 3.72) * mm});
            skLineSegment(sketch, "E693", {"start": v(-20.29, 3.72) * mm, "end": v(-20.18, 3.65) * mm});
            skLineSegment(sketch, "E694", {"start": v(-20.18, 3.65) * mm, "end": v(-20.08, 3.59) * mm});
            skLineSegment(sketch, "E695", {"start": v(-20.08, 3.59) * mm, "end": v(-19.96, 3.52) * mm});
            skLineSegment(sketch, "E696", {"start": v(-19.96, 3.52) * mm, "end": v(-19.85, 3.45) * mm});
            skLineSegment(sketch, "E697", {"start": v(-19.85, 3.45) * mm, "end": v(-19.72, 3.39) * mm});
            skLineSegment(sketch, "E698", {"start": v(-19.72, 3.39) * mm, "end": v(-19.6, 3.32) * mm});
            skLineSegment(sketch, "E699", {"start": v(-19.6, 3.32) * mm, "end": v(-19.45, 3.25) * mm});
            skLineSegment(sketch, "E700", {"start": v(-19.45, 3.25) * mm, "end": v(-19.28, 3.18) * mm});
            skLineSegment(sketch, "E701", {"start": v(-19.28, 3.18) * mm, "end": v(-18.98, 3.07) * mm});
            skLineSegment(sketch, "E702", {"start": v(-18.98, 3.07) * mm, "end": v(-18.96, 3.07) * mm});
            skLineSegment(sketch, "E703", {"start": v(-18.96, 3.07) * mm, "end": v(-19.07, 2.27) * mm});
            skLineSegment(sketch, "E704", {"start": v(-19.07, 2.27) * mm, "end": v(-19.09, 2.28) * mm});
            skLineSegment(sketch, "E705", {"start": v(-19.09, 2.28) * mm, "end": v(-19.41, 2.25) * mm});
            skLineSegment(sketch, "E706", {"start": v(-19.41, 2.25) * mm, "end": v(-19.6, 2.23) * mm});
            skLineSegment(sketch, "E707", {"start": v(-19.6, 2.23) * mm, "end": v(-19.75, 2.2) * mm});
            skLineSegment(sketch, "E708", {"start": v(-19.75, 2.2) * mm, "end": v(-19.9, 2.18) * mm});
            skLineSegment(sketch, "E709", {"start": v(-19.9, 2.18) * mm, "end": v(-20.03, 2.15) * mm});
            skLineSegment(sketch, "E710", {"start": v(-20.03, 2.15) * mm, "end": v(-20.16, 2.11) * mm});
            skLineSegment(sketch, "E711", {"start": v(-20.16, 2.11) * mm, "end": v(-20.29, 2.08) * mm});
            skLineSegment(sketch, "E712", {"start": v(-20.29, 2.08) * mm, "end": v(-20.4, 2.05) * mm});
            skLineSegment(sketch, "E713", {"start": v(-20.4, 2.05) * mm, "end": v(-20.53, 2.01) * mm});
            skLineSegment(sketch, "E714", {"start": v(-20.53, 2.01) * mm, "end": v(-20.64, 1.98) * mm});
            skLineSegment(sketch, "E715", {"start": v(-20.64, 1.98) * mm, "end": v(-20.76, 1.94) * mm});
            skLineSegment(sketch, "E716", {"start": v(-20.76, 1.94) * mm, "end": v(-20.87, 1.9) * mm});
            skLineSegment(sketch, "E717", {"start": v(-20.87, 1.9) * mm, "end": v(-20.98, 1.86) * mm});
            skLineSegment(sketch, "E718", {"start": v(-20.98, 1.86) * mm, "end": v(-21.09, 1.82) * mm});
            skLineSegment(sketch, "E719", {"start": v(-21.09, 1.82) * mm, "end": v(-21.13, 1.13) * mm});
            skLineSegment(sketch, "E720", {"start": v(-21.13, 1.13) * mm, "end": v(-21.03, 1.08) * mm});
            skLineSegment(sketch, "E721", {"start": v(-21.03, 1.08) * mm, "end": v(-20.93, 1.02) * mm});
            skLineSegment(sketch, "E722", {"start": v(-20.93, 1.02) * mm, "end": v(-20.82, 0.97) * mm});
            skLineSegment(sketch, "E723", {"start": v(-20.82, 0.97) * mm, "end": v(-20.72, 0.91) * mm});
            skLineSegment(sketch, "E724", {"start": v(-20.72, 0.91) * mm, "end": v(-20.6, 0.86) * mm});
            skLineSegment(sketch, "E725", {"start": v(-20.6, 0.86) * mm, "end": v(-20.5, 0.81) * mm});
            skLineSegment(sketch, "E726", {"start": v(-20.5, 0.81) * mm, "end": v(-20.38, 0.76) * mm});
            skLineSegment(sketch, "E727", {"start": v(-20.38, 0.76) * mm, "end": v(-20.26, 0.71) * mm});
            skLineSegment(sketch, "E728", {"start": v(-20.26, 0.71) * mm, "end": v(-20.14, 0.66) * mm});
            skLineSegment(sketch, "E729", {"start": v(-20.14, 0.66) * mm, "end": v(-20, 0.61) * mm});
            skLineSegment(sketch, "E730", {"start": v(-20, 0.61) * mm, "end": v(-19.86, 0.56) * mm});
            skLineSegment(sketch, "E731", {"start": v(-19.86, 0.56) * mm, "end": v(-19.71, 0.52) * mm});
            skLineSegment(sketch, "E732", {"start": v(-19.71, 0.52) * mm, "end": v(-19.54, 0.47) * mm});
            skLineSegment(sketch, "E733", {"start": v(-19.54, 0.47) * mm, "end": v(-19.22, 0.4) * mm});
            skLineSegment(sketch, "E734", {"start": v(-19.22, 0.4) * mm, "end": v(-19.2, 0.4) * mm});
            skLineSegment(sketch, "E735", {"start": v(-19.2, 0.4) * mm, "end": v(-19.2, -0.4) * mm});
            skLineSegment(sketch, "E736", {"start": v(-19.2, -0.4) * mm, "end": v(-19.22, -0.4) * mm});
            skLineSegment(sketch, "E737", {"start": v(-19.22, -0.4) * mm, "end": v(-19.54, -0.47) * mm});
            skLineSegment(sketch, "E738", {"start": v(-19.54, -0.47) * mm, "end": v(-19.71, -0.52) * mm});
            skLineSegment(sketch, "E739", {"start": v(-19.71, -0.52) * mm, "end": v(-19.86, -0.56) * mm});
            skLineSegment(sketch, "E740", {"start": v(-19.86, -0.56) * mm, "end": v(-20, -0.61) * mm});
            skLineSegment(sketch, "E741", {"start": v(-20, -0.61) * mm, "end": v(-20.14, -0.66) * mm});
            skLineSegment(sketch, "E742", {"start": v(-20.14, -0.66) * mm, "end": v(-20.26, -0.71) * mm});
            skLineSegment(sketch, "E743", {"start": v(-20.26, -0.71) * mm, "end": v(-20.38, -0.76) * mm});
            skLineSegment(sketch, "E744", {"start": v(-20.38, -0.76) * mm, "end": v(-20.5, -0.81) * mm});
            skLineSegment(sketch, "E745", {"start": v(-20.5, -0.81) * mm, "end": v(-20.6, -0.86) * mm});
            skLineSegment(sketch, "E746", {"start": v(-20.6, -0.86) * mm, "end": v(-20.72, -0.91) * mm});
            skLineSegment(sketch, "E747", {"start": v(-20.72, -0.91) * mm, "end": v(-20.82, -0.97) * mm});
            skLineSegment(sketch, "E748", {"start": v(-20.82, -0.97) * mm, "end": v(-20.93, -1.02) * mm});
            skLineSegment(sketch, "E749", {"start": v(-20.93, -1.02) * mm, "end": v(-21.03, -1.08) * mm});
            skLineSegment(sketch, "E750", {"start": v(-21.03, -1.08) * mm, "end": v(-21.13, -1.13) * mm});
            skLineSegment(sketch, "E751", {"start": v(-21.13, -1.13) * mm, "end": v(-21.09, -1.82) * mm});
            skLineSegment(sketch, "E752", {"start": v(-21.09, -1.82) * mm, "end": v(-20.98, -1.86) * mm});
            skLineSegment(sketch, "E753", {"start": v(-20.98, -1.86) * mm, "end": v(-20.87, -1.9) * mm});
            skLineSegment(sketch, "E754", {"start": v(-20.87, -1.9) * mm, "end": v(-20.76, -1.94) * mm});
            skLineSegment(sketch, "E755", {"start": v(-20.76, -1.94) * mm, "end": v(-20.64, -1.98) * mm});
            skLineSegment(sketch, "E756", {"start": v(-20.64, -1.98) * mm, "end": v(-20.53, -2.01) * mm});
            skLineSegment(sketch, "E757", {"start": v(-20.53, -2.01) * mm, "end": v(-20.4, -2.05) * mm});
            skLineSegment(sketch, "E758", {"start": v(-20.4, -2.05) * mm, "end": v(-20.29, -2.08) * mm});
            skLineSegment(sketch, "E759", {"start": v(-20.29, -2.08) * mm, "end": v(-20.16, -2.11) * mm});
            skLineSegment(sketch, "E760", {"start": v(-20.16, -2.11) * mm, "end": v(-20.03, -2.15) * mm});
            skLineSegment(sketch, "E761", {"start": v(-20.03, -2.15) * mm, "end": v(-19.9, -2.18) * mm});
            skLineSegment(sketch, "E762", {"start": v(-19.9, -2.18) * mm, "end": v(-19.75, -2.2) * mm});
            skLineSegment(sketch, "E763", {"start": v(-19.75, -2.2) * mm, "end": v(-19.6, -2.23) * mm});
            skLineSegment(sketch, "E764", {"start": v(-19.6, -2.23) * mm, "end": v(-19.41, -2.25) * mm});
            skLineSegment(sketch, "E765", {"start": v(-19.41, -2.25) * mm, "end": v(-19.09, -2.28) * mm});
            skLineSegment(sketch, "E766", {"start": v(-19.09, -2.28) * mm, "end": v(-19.07, -2.27) * mm});
            skLineSegment(sketch, "E767", {"start": v(-19.07, -2.27) * mm, "end": v(-18.96, -3.07) * mm});
            skLineSegment(sketch, "E768", {"start": v(-18.96, -3.07) * mm, "end": v(-18.98, -3.07) * mm});
            skLineSegment(sketch, "E769", {"start": v(-18.98, -3.07) * mm, "end": v(-19.28, -3.18) * mm});
            skLineSegment(sketch, "E770", {"start": v(-19.28, -3.18) * mm, "end": v(-19.45, -3.25) * mm});
            skLineSegment(sketch, "E771", {"start": v(-19.45, -3.25) * mm, "end": v(-19.6, -3.32) * mm});
            skLineSegment(sketch, "E772", {"start": v(-19.6, -3.32) * mm, "end": v(-19.72, -3.39) * mm});
            skLineSegment(sketch, "E773", {"start": v(-19.72, -3.39) * mm, "end": v(-19.85, -3.45) * mm});
            skLineSegment(sketch, "E774", {"start": v(-19.85, -3.45) * mm, "end": v(-19.96, -3.52) * mm});
            skLineSegment(sketch, "E775", {"start": v(-19.96, -3.52) * mm, "end": v(-20.08, -3.59) * mm});
            skLineSegment(sketch, "E776", {"start": v(-20.08, -3.59) * mm, "end": v(-20.18, -3.65) * mm});
            skLineSegment(sketch, "E777", {"start": v(-20.18, -3.65) * mm, "end": v(-20.29, -3.72) * mm});
            skLineSegment(sketch, "E778", {"start": v(-20.29, -3.72) * mm, "end": v(-20.39, -3.79) * mm});
            skLineSegment(sketch, "E779", {"start": v(-20.39, -3.79) * mm, "end": v(-20.49, -3.85) * mm});
            skLineSegment(sketch, "E780", {"start": v(-20.49, -3.85) * mm, "end": v(-20.58, -3.92) * mm});
            skLineSegment(sketch, "E781", {"start": v(-20.58, -3.92) * mm, "end": v(-20.68, -4) * mm});
            skLineSegment(sketch, "E782", {"start": v(-20.68, -4) * mm, "end": v(-20.77, -4.06) * mm});
            skLineSegment(sketch, "E783", {"start": v(-20.77, -4.06) * mm, "end": v(-20.63, -4.74) * mm});
            skLineSegment(sketch, "E784", {"start": v(-20.63, -4.74) * mm, "end": v(-20.51, -4.76) * mm});
            skLineSegment(sketch, "E785", {"start": v(-20.51, -4.76) * mm, "end": v(-20.4, -4.78) * mm});
            skLineSegment(sketch, "E786", {"start": v(-20.4, -4.78) * mm, "end": v(-20.29, -4.8) * mm});
            skLineSegment(sketch, "E787", {"start": v(-20.29, -4.8) * mm, "end": v(-20.17, -4.83) * mm});
            skLineSegment(sketch, "E788", {"start": v(-20.17, -4.83) * mm, "end": v(-20.05, -4.85) * mm});
            skLineSegment(sketch, "E789", {"start": v(-20.05, -4.85) * mm, "end": v(-19.93, -4.87) * mm});
            skLineSegment(sketch, "E790", {"start": v(-19.93, -4.87) * mm, "end": v(-19.8, -4.88) * mm});
            skLineSegment(sketch, "E791", {"start": v(-19.8, -4.88) * mm, "end": v(-19.67, -4.9) * mm});
            skLineSegment(sketch, "E792", {"start": v(-19.67, -4.9) * mm, "end": v(-19.54, -4.91) * mm});
            skLineSegment(sketch, "E793", {"start": v(-19.54, -4.91) * mm, "end": v(-19.4, -4.92) * mm});
            skLineSegment(sketch, "E794", {"start": v(-19.4, -4.92) * mm, "end": v(-19.25, -4.93) * mm});
            skLineSegment(sketch, "E795", {"start": v(-19.25, -4.93) * mm, "end": v(-19.1, -4.93) * mm});
            skLineSegment(sketch, "E796", {"start": v(-19.1, -4.93) * mm, "end": v(-18.9, -4.93) * mm});
            skLineSegment(sketch, "E797", {"start": v(-18.9, -4.93) * mm, "end": v(-18.58, -4.9) * mm});
            skLineSegment(sketch, "E798", {"start": v(-18.58, -4.9) * mm, "end": v(-18.57, -4.9) * mm});
            skLineSegment(sketch, "E799", {"start": v(-18.57, -4.9) * mm, "end": v(-18.35, -5.67) * mm});
            skLineSegment(sketch, "E800", {"start": v(-18.35, -5.67) * mm, "end": v(-18.36, -5.68) * mm});
            skLineSegment(sketch, "E801", {"start": v(-18.36, -5.68) * mm, "end": v(-18.65, -5.83) * mm});
            skLineSegment(sketch, "E802", {"start": v(-18.65, -5.83) * mm, "end": v(-18.8, -5.93) * mm});
            skLineSegment(sketch, "E803", {"start": v(-18.8, -5.93) * mm, "end": v(-18.94, -6.01) * mm});
            skLineSegment(sketch, "E804", {"start": v(-18.94, -6.01) * mm, "end": v(-19.06, -6.1) * mm});
            skLineSegment(sketch, "E805", {"start": v(-19.06, -6.1) * mm, "end": v(-19.17, -6.18) * mm});
            skLineSegment(sketch, "E806", {"start": v(-19.17, -6.18) * mm, "end": v(-19.28, -6.26) * mm});
            skLineSegment(sketch, "E807", {"start": v(-19.28, -6.26) * mm, "end": v(-19.38, -6.34) * mm});
            skLineSegment(sketch, "E808", {"start": v(-19.38, -6.34) * mm, "end": v(-19.48, -6.42) * mm});
            skLineSegment(sketch, "E809", {"start": v(-19.48, -6.42) * mm, "end": v(-19.57, -6.5) * mm});
            skLineSegment(sketch, "E810", {"start": v(-19.57, -6.5) * mm, "end": v(-19.66, -6.59) * mm});
            skLineSegment(sketch, "E811", {"start": v(-19.66, -6.59) * mm, "end": v(-19.75, -6.67) * mm});
            skLineSegment(sketch, "E812", {"start": v(-19.75, -6.67) * mm, "end": v(-19.84, -6.75) * mm});
            skLineSegment(sketch, "E813", {"start": v(-19.84, -6.75) * mm, "end": v(-19.92, -6.83) * mm});
            skLineSegment(sketch, "E814", {"start": v(-19.92, -6.83) * mm, "end": v(-20, -6.9) * mm});
            skLineSegment(sketch, "E815", {"start": v(-20, -6.9) * mm, "end": v(-19.77, -7.56) * mm});
            skLineSegment(sketch, "E816", {"start": v(-19.77, -7.56) * mm, "end": v(-19.65, -7.57) * mm});
            skLineSegment(sketch, "E817", {"start": v(-19.65, -7.57) * mm, "end": v(-19.54, -7.57) * mm});
            skLineSegment(sketch, "E818", {"start": v(-19.54, -7.57) * mm, "end": v(-19.42, -7.58) * mm});
            skLineSegment(sketch, "E819", {"start": v(-19.42, -7.58) * mm, "end": v(-19.3, -7.59) * mm});
            skLineSegment(sketch, "E820", {"start": v(-19.3, -7.59) * mm, "end": v(-19.18, -7.59) * mm});
            skLineSegment(sketch, "E821", {"start": v(-19.18, -7.59) * mm, "end": v(-19.05, -7.6) * mm});
            skLineSegment(sketch, "E822", {"start": v(-19.05, -7.6) * mm, "end": v(-18.93, -7.59) * mm});
            skLineSegment(sketch, "E823", {"start": v(-18.93, -7.59) * mm, "end": v(-18.8, -7.59) * mm});
            skLineSegment(sketch, "E824", {"start": v(-18.8, -7.59) * mm, "end": v(-18.66, -7.58) * mm});
            skLineSegment(sketch, "E825", {"start": v(-18.66, -7.58) * mm, "end": v(-18.53, -7.57) * mm});
            skLineSegment(sketch, "E826", {"start": v(-18.53, -7.57) * mm, "end": v(-18.38, -7.56) * mm});
            skLineSegment(sketch, "E827", {"start": v(-18.38, -7.56) * mm, "end": v(-18.22, -7.54) * mm});
            skLineSegment(sketch, "E828", {"start": v(-18.22, -7.54) * mm, "end": v(-18.04, -7.51) * mm});
            skLineSegment(sketch, "E829", {"start": v(-18.04, -7.51) * mm, "end": v(-17.72, -7.45) * mm});
            skLineSegment(sketch, "E830", {"start": v(-17.72, -7.45) * mm, "end": v(-17.7, -7.44) * mm});
            skLineSegment(sketch, "E831", {"start": v(-17.7, -7.44) * mm, "end": v(-17.38, -8.17) * mm});
            skLineSegment(sketch, "E832", {"start": v(-17.38, -8.17) * mm, "end": v(-17.4, -8.18) * mm});
            skLineSegment(sketch, "E833", {"start": v(-17.4, -8.18) * mm, "end": v(-17.66, -8.37) * mm});
            skLineSegment(sketch, "E834", {"start": v(-17.66, -8.37) * mm, "end": v(-17.8, -8.48) * mm});
            skLineSegment(sketch, "E835", {"start": v(-17.8, -8.48) * mm, "end": v(-17.92, -8.6) * mm});
            skLineSegment(sketch, "E836", {"start": v(-17.92, -8.6) * mm, "end": v(-18.03, -8.7) * mm});
            skLineSegment(sketch, "E837", {"start": v(-18.03, -8.7) * mm, "end": v(-18.13, -8.79) * mm});
            skLineSegment(sketch, "E838", {"start": v(-18.13, -8.79) * mm, "end": v(-18.22, -8.88) * mm});
            skLineSegment(sketch, "E839", {"start": v(-18.22, -8.88) * mm, "end": v(-18.3, -8.98) * mm});
            skLineSegment(sketch, "E840", {"start": v(-18.3, -8.98) * mm, "end": v(-18.4, -9.07) * mm});
            skLineSegment(sketch, "E841", {"start": v(-18.4, -9.07) * mm, "end": v(-18.48, -9.16) * mm});
            skLineSegment(sketch, "E842", {"start": v(-18.48, -9.16) * mm, "end": v(-18.56, -9.26) * mm});
            skLineSegment(sketch, "E843", {"start": v(-18.56, -9.26) * mm, "end": v(-18.63, -9.35) * mm});
            skLineSegment(sketch, "E844", {"start": v(-18.63, -9.35) * mm, "end": v(-18.7, -9.44) * mm});
            skLineSegment(sketch, "E845", {"start": v(-18.7, -9.44) * mm, "end": v(-18.78, -9.53) * mm});
            skLineSegment(sketch, "E846", {"start": v(-18.78, -9.53) * mm, "end": v(-18.85, -9.62) * mm});
            skLineSegment(sketch, "E847", {"start": v(-18.85, -9.62) * mm, "end": v(-18.52, -10.23) * mm});
            skLineSegment(sketch, "E848", {"start": v(-18.52, -10.23) * mm, "end": v(-18.4, -10.23) * mm});
            skLineSegment(sketch, "E849", {"start": v(-18.4, -10.23) * mm, "end": v(-18.3, -10.22) * mm});
            skLineSegment(sketch, "E850", {"start": v(-18.3, -10.22) * mm, "end": v(-18.18, -10.2) * mm});
            skLineSegment(sketch, "E851", {"start": v(-18.18, -10.2) * mm, "end": v(-18.06, -10.2) * mm});
            skLineSegment(sketch, "E852", {"start": v(-18.06, -10.2) * mm, "end": v(-17.94, -10.18) * mm});
            skLineSegment(sketch, "E853", {"start": v(-17.94, -10.18) * mm, "end": v(-17.81, -10.17) * mm});
            skLineSegment(sketch, "E854", {"start": v(-17.81, -10.17) * mm, "end": v(-17.69, -10.15) * mm});
            skLineSegment(sketch, "E855", {"start": v(-17.69, -10.15) * mm, "end": v(-17.56, -10.13) * mm});
            skLineSegment(sketch, "E856", {"start": v(-17.56, -10.13) * mm, "end": v(-17.43, -10.1) * mm});
            skLineSegment(sketch, "E857", {"start": v(-17.43, -10.1) * mm, "end": v(-17.3, -10.07) * mm});
            skLineSegment(sketch, "E858", {"start": v(-17.3, -10.07) * mm, "end": v(-17.15, -10.04) * mm});
            skLineSegment(sketch, "E859", {"start": v(-17.15, -10.04) * mm, "end": v(-17, -10) * mm});
            skLineSegment(sketch, "E860", {"start": v(-17, -10) * mm, "end": v(-16.82, -9.95) * mm});
            skLineSegment(sketch, "E861", {"start": v(-16.82, -9.95) * mm, "end": v(-16.51, -9.84) * mm});
            skLineSegment(sketch, "E862", {"start": v(-16.51, -9.84) * mm, "end": v(-16.5, -9.83) * mm});
            skLineSegment(sketch, "E863", {"start": v(-16.5, -9.83) * mm, "end": v(-16.07, -10.5) * mm});
            skLineSegment(sketch, "E864", {"start": v(-16.07, -10.5) * mm, "end": v(-16.09, -10.52) * mm});
            skLineSegment(sketch, "E865", {"start": v(-16.09, -10.52) * mm, "end": v(-16.32, -10.74) * mm});
            skLineSegment(sketch, "E866", {"start": v(-16.32, -10.74) * mm, "end": v(-16.45, -10.88) * mm});
            skLineSegment(sketch, "E867", {"start": v(-16.45, -10.88) * mm, "end": v(-16.55, -11) * mm});
            skLineSegment(sketch, "E868", {"start": v(-16.55, -11) * mm, "end": v(-16.64, -11.11) * mm});
            skLineSegment(sketch, "E869", {"start": v(-16.64, -11.11) * mm, "end": v(-16.73, -11.22) * mm});
            skLineSegment(sketch, "E870", {"start": v(-16.73, -11.22) * mm, "end": v(-16.8, -11.33) * mm});
            skLineSegment(sketch, "E871", {"start": v(-16.8, -11.33) * mm, "end": v(-16.88, -11.44) * mm});
            skLineSegment(sketch, "E872", {"start": v(-16.88, -11.44) * mm, "end": v(-16.95, -11.54) * mm});
            skLineSegment(sketch, "E873", {"start": v(-16.95, -11.54) * mm, "end": v(-17.02, -11.64) * mm});
            skLineSegment(sketch, "E874", {"start": v(-17.02, -11.64) * mm, "end": v(-17.09, -11.75) * mm});
            skLineSegment(sketch, "E875", {"start": v(-17.09, -11.75) * mm, "end": v(-17.15, -11.85) * mm});
            skLineSegment(sketch, "E876", {"start": v(-17.15, -11.85) * mm, "end": v(-17.21, -11.95) * mm});
            skLineSegment(sketch, "E877", {"start": v(-17.21, -11.95) * mm, "end": v(-17.27, -12.05) * mm});
            skLineSegment(sketch, "E878", {"start": v(-17.27, -12.05) * mm, "end": v(-17.33, -12.15) * mm});
            skLineSegment(sketch, "E879", {"start": v(-17.33, -12.15) * mm, "end": v(-16.92, -12.7) * mm});
            skLineSegment(sketch, "E880", {"start": v(-16.92, -12.7) * mm, "end": v(-16.8, -12.69) * mm});
            skLineSegment(sketch, "E881", {"start": v(-16.8, -12.69) * mm, "end": v(-16.7, -12.66) * mm});
            skLineSegment(sketch, "E882", {"start": v(-16.7, -12.66) * mm, "end": v(-16.58, -12.64) * mm});
            skLineSegment(sketch, "E883", {"start": v(-16.58, -12.64) * mm, "end": v(-16.46, -12.6) * mm});
            skLineSegment(sketch, "E884", {"start": v(-16.46, -12.6) * mm, "end": v(-16.34, -12.58) * mm});
            skLineSegment(sketch, "E885", {"start": v(-16.34, -12.58) * mm, "end": v(-16.22, -12.54) * mm});
            skLineSegment(sketch, "E886", {"start": v(-16.22, -12.54) * mm, "end": v(-16.1, -12.5) * mm});
            skLineSegment(sketch, "E887", {"start": v(-16.1, -12.5) * mm, "end": v(-15.98, -12.47) * mm});
            skLineSegment(sketch, "E888", {"start": v(-15.98, -12.47) * mm, "end": v(-15.85, -12.43) * mm});
            skLineSegment(sketch, "E889", {"start": v(-15.85, -12.43) * mm, "end": v(-15.72, -12.38) * mm});
            skLineSegment(sketch, "E890", {"start": v(-15.72, -12.38) * mm, "end": v(-15.58, -12.33) * mm});
            skLineSegment(sketch, "E891", {"start": v(-15.58, -12.33) * mm, "end": v(-15.44, -12.27) * mm});
            skLineSegment(sketch, "E892", {"start": v(-15.44, -12.27) * mm, "end": v(-15.27, -12.2) * mm});
            skLineSegment(sketch, "E893", {"start": v(-15.27, -12.2) * mm, "end": v(-14.98, -12.04) * mm});
            skLineSegment(sketch, "E894", {"start": v(-14.98, -12.04) * mm, "end": v(-14.97, -12.03) * mm});
            skLineSegment(sketch, "E895", {"start": v(-14.97, -12.03) * mm, "end": v(-14.45, -12.64) * mm});
            skLineSegment(sketch, "E896", {"start": v(-14.45, -12.64) * mm, "end": v(-14.47, -12.65) * mm});
            skLineSegment(sketch, "E897", {"start": v(-14.47, -12.65) * mm, "end": v(-14.67, -12.9) * mm});
            skLineSegment(sketch, "E898", {"start": v(-14.67, -12.9) * mm, "end": v(-14.77, -13.06) * mm});
            skLineSegment(sketch, "E899", {"start": v(-14.77, -13.06) * mm, "end": v(-14.86, -13.2) * mm});
            skLineSegment(sketch, "E900", {"start": v(-14.86, -13.2) * mm, "end": v(-14.93, -13.32) * mm});
            skLineSegment(sketch, "E901", {"start": v(-14.93, -13.32) * mm, "end": v(-15, -13.44) * mm});
            skLineSegment(sketch, "E902", {"start": v(-15, -13.44) * mm, "end": v(-15.07, -13.56) * mm});
            skLineSegment(sketch, "E903", {"start": v(-15.07, -13.56) * mm, "end": v(-15.13, -13.67) * mm});
            skLineSegment(sketch, "E904", {"start": v(-15.13, -13.67) * mm, "end": v(-15.18, -13.79) * mm});
            skLineSegment(sketch, "E905", {"start": v(-15.18, -13.79) * mm, "end": v(-15.24, -13.9) * mm});
            skLineSegment(sketch, "E906", {"start": v(-15.24, -13.9) * mm, "end": v(-15.29, -14) * mm});
            skLineSegment(sketch, "E907", {"start": v(-15.29, -14) * mm, "end": v(-15.33, -14.12) * mm});
            skLineSegment(sketch, "E908", {"start": v(-15.33, -14.12) * mm, "end": v(-15.38, -14.23) * mm});
            skLineSegment(sketch, "E909", {"start": v(-15.38, -14.23) * mm, "end": v(-15.42, -14.33) * mm});
            skLineSegment(sketch, "E910", {"start": v(-15.42, -14.33) * mm, "end": v(-15.47, -14.44) * mm});
            skLineSegment(sketch, "E911", {"start": v(-15.47, -14.44) * mm, "end": v(-14.99, -14.94) * mm});
            skLineSegment(sketch, "E912", {"start": v(-14.99, -14.94) * mm, "end": v(-14.88, -14.9) * mm});
            skLineSegment(sketch, "E913", {"start": v(-14.88, -14.9) * mm, "end": v(-14.77, -14.86) * mm});
            skLineSegment(sketch, "E914", {"start": v(-14.77, -14.86) * mm, "end": v(-14.66, -14.82) * mm});
            skLineSegment(sketch, "E915", {"start": v(-14.66, -14.82) * mm, "end": v(-14.55, -14.77) * mm});
            skLineSegment(sketch, "E916", {"start": v(-14.55, -14.77) * mm, "end": v(-14.43, -14.73) * mm});
            skLineSegment(sketch, "E917", {"start": v(-14.43, -14.73) * mm, "end": v(-14.32, -14.68) * mm});
            skLineSegment(sketch, "E918", {"start": v(-14.32, -14.68) * mm, "end": v(-14.2, -14.63) * mm});
            skLineSegment(sketch, "E919", {"start": v(-14.2, -14.63) * mm, "end": v(-14.09, -14.57) * mm});
            skLineSegment(sketch, "E920", {"start": v(-14.09, -14.57) * mm, "end": v(-13.97, -14.51) * mm});
            skLineSegment(sketch, "E921", {"start": v(-13.97, -14.51) * mm, "end": v(-13.85, -14.45) * mm});
            skLineSegment(sketch, "E922", {"start": v(-13.85, -14.45) * mm, "end": v(-13.72, -14.37) * mm});
            skLineSegment(sketch, "E923", {"start": v(-13.72, -14.37) * mm, "end": v(-13.58, -14.3) * mm});
            skLineSegment(sketch, "E924", {"start": v(-13.58, -14.3) * mm, "end": v(-13.42, -14.2) * mm});
            skLineSegment(sketch, "E925", {"start": v(-13.42, -14.2) * mm, "end": v(-13.16, -14) * mm});
            skLineSegment(sketch, "E926", {"start": v(-13.16, -14) * mm, "end": v(-13.15, -13.99) * mm});
            skLineSegment(sketch, "E927", {"start": v(-13.15, -13.99) * mm, "end": v(-12.55, -14.53) * mm});
            skLineSegment(sketch, "E928", {"start": v(-12.55, -14.53) * mm, "end": v(-12.57, -14.54) * mm});
            skLineSegment(sketch, "E929", {"start": v(-12.57, -14.54) * mm, "end": v(-12.73, -14.82) * mm});
            skLineSegment(sketch, "E930", {"start": v(-12.73, -14.82) * mm, "end": v(-12.81, -14.99) * mm});
            skLineSegment(sketch, "E931", {"start": v(-12.81, -14.99) * mm, "end": v(-12.88, -15.13) * mm});
            skLineSegment(sketch, "E932", {"start": v(-12.88, -15.13) * mm, "end": v(-12.93, -15.27) * mm});
            skLineSegment(sketch, "E933", {"start": v(-12.93, -15.27) * mm, "end": v(-12.99, -15.4) * mm});
            skLineSegment(sketch, "E934", {"start": v(-12.99, -15.4) * mm, "end": v(-13.03, -15.52) * mm});
            skLineSegment(sketch, "E935", {"start": v(-13.03, -15.52) * mm, "end": v(-13.08, -15.64) * mm});
            skLineSegment(sketch, "E936", {"start": v(-13.08, -15.64) * mm, "end": v(-13.12, -15.76) * mm});
            skLineSegment(sketch, "E937", {"start": v(-13.12, -15.76) * mm, "end": v(-13.15, -15.88) * mm});
            skLineSegment(sketch, "E938", {"start": v(-13.15, -15.88) * mm, "end": v(-13.19, -16) * mm});
            skLineSegment(sketch, "E939", {"start": v(-13.19, -16) * mm, "end": v(-13.22, -16.11) * mm});
            skLineSegment(sketch, "E940", {"start": v(-13.22, -16.11) * mm, "end": v(-13.25, -16.23) * mm});
            skLineSegment(sketch, "E941", {"start": v(-13.25, -16.23) * mm, "end": v(-13.28, -16.34) * mm});
            skLineSegment(sketch, "E942", {"start": v(-13.28, -16.34) * mm, "end": v(-13.3, -16.45) * mm});
            skLineSegment(sketch, "E943", {"start": v(-13.3, -16.45) * mm, "end": v(-12.76, -16.88) * mm});
            skLineSegment(sketch, "E944", {"start": v(-12.76, -16.88) * mm, "end": v(-12.66, -16.82) * mm});
            skLineSegment(sketch, "E945", {"start": v(-12.66, -16.82) * mm, "end": v(-12.56, -16.77) * mm});
            skLineSegment(sketch, "E946", {"start": v(-12.56, -16.77) * mm, "end": v(-12.45, -16.71) * mm});
            skLineSegment(sketch, "E947", {"start": v(-12.45, -16.71) * mm, "end": v(-12.35, -16.65) * mm});
            skLineSegment(sketch, "E948", {"start": v(-12.35, -16.65) * mm, "end": v(-12.24, -16.6) * mm});
            skLineSegment(sketch, "E949", {"start": v(-12.24, -16.6) * mm, "end": v(-12.14, -16.53) * mm});
            skLineSegment(sketch, "E950", {"start": v(-12.14, -16.53) * mm, "end": v(-12.03, -16.46) * mm});
            skLineSegment(sketch, "E951", {"start": v(-12.03, -16.46) * mm, "end": v(-11.92, -16.39) * mm});
            skLineSegment(sketch, "E952", {"start": v(-11.92, -16.39) * mm, "end": v(-11.81, -16.31) * mm});
            skLineSegment(sketch, "E953", {"start": v(-11.81, -16.31) * mm, "end": v(-11.7, -16.23) * mm});
            skLineSegment(sketch, "E954", {"start": v(-11.7, -16.23) * mm, "end": v(-11.58, -16.14) * mm});
            skLineSegment(sketch, "E955", {"start": v(-11.58, -16.14) * mm, "end": v(-11.46, -16.04) * mm});
            skLineSegment(sketch, "E956", {"start": v(-11.46, -16.04) * mm, "end": v(-11.32, -15.92) * mm});
            skLineSegment(sketch, "E957", {"start": v(-11.32, -15.92) * mm, "end": v(-11.09, -15.7) * mm});
            skLineSegment(sketch, "E958", {"start": v(-11.09, -15.7) * mm, "end": v(-11.07, -15.68) * mm});
            skLineSegment(sketch, "E959", {"start": v(-11.07, -15.68) * mm, "end": v(-10.41, -16.13) * mm});
            skLineSegment(sketch, "E960", {"start": v(-10.41, -16.13) * mm, "end": v(-10.42, -16.15) * mm});
            skLineSegment(sketch, "E961", {"start": v(-10.42, -16.15) * mm, "end": v(-10.54, -16.45) * mm});
            skLineSegment(sketch, "E962", {"start": v(-10.54, -16.45) * mm, "end": v(-10.6, -16.62) * mm});
            skLineSegment(sketch, "E963", {"start": v(-10.6, -16.62) * mm, "end": v(-10.65, -16.77) * mm});
            skLineSegment(sketch, "E964", {"start": v(-10.65, -16.77) * mm, "end": v(-10.68, -16.92) * mm});
            skLineSegment(sketch, "E965", {"start": v(-10.68, -16.92) * mm, "end": v(-10.72, -17.05) * mm});
            skLineSegment(sketch, "E966", {"start": v(-10.72, -17.05) * mm, "end": v(-10.75, -17.18) * mm});
            skLineSegment(sketch, "E967", {"start": v(-10.75, -17.18) * mm, "end": v(-10.77, -17.3) * mm});
            skLineSegment(sketch, "E968", {"start": v(-10.77, -17.3) * mm, "end": v(-10.8, -17.43) * mm});
            skLineSegment(sketch, "E969", {"start": v(-10.8, -17.43) * mm, "end": v(-10.82, -17.56) * mm});
            skLineSegment(sketch, "E970", {"start": v(-10.82, -17.56) * mm, "end": v(-10.83, -17.68) * mm});
            skLineSegment(sketch, "E971", {"start": v(-10.83, -17.68) * mm, "end": v(-10.85, -17.8) * mm});
            skLineSegment(sketch, "E972", {"start": v(-10.85, -17.8) * mm, "end": v(-10.86, -17.91) * mm});
            skLineSegment(sketch, "E973", {"start": v(-10.86, -17.91) * mm, "end": v(-10.88, -18.03) * mm});
            skLineSegment(sketch, "E974", {"start": v(-10.88, -18.03) * mm, "end": v(-10.89, -18.14) * mm});
            skLineSegment(sketch, "E975", {"start": v(-10.89, -18.14) * mm, "end": v(-10.29, -18.49) * mm});
            skLineSegment(sketch, "E976", {"start": v(-10.29, -18.49) * mm, "end": v(-10.2, -18.42) * mm});
            skLineSegment(sketch, "E977", {"start": v(-10.2, -18.42) * mm, "end": v(-10.1, -18.35) * mm});
            skLineSegment(sketch, "E978", {"start": v(-10.1, -18.35) * mm, "end": v(-10, -18.28) * mm});
            skLineSegment(sketch, "E979", {"start": v(-10, -18.28) * mm, "end": v(-9.91, -18.2) * mm});
            skLineSegment(sketch, "E980", {"start": v(-9.91, -18.2) * mm, "end": v(-9.82, -18.13) * mm});
            skLineSegment(sketch, "E981", {"start": v(-9.82, -18.13) * mm, "end": v(-9.72, -18.05) * mm});
            skLineSegment(sketch, "E982", {"start": v(-9.72, -18.05) * mm, "end": v(-9.62, -17.97) * mm});
            skLineSegment(sketch, "E983", {"start": v(-9.62, -17.97) * mm, "end": v(-9.53, -17.89) * mm});
            skLineSegment(sketch, "E984", {"start": v(-9.53, -17.89) * mm, "end": v(-9.43, -17.8) * mm});
            skLineSegment(sketch, "E985", {"start": v(-9.43, -17.8) * mm, "end": v(-9.33, -17.7) * mm});
            skLineSegment(sketch, "E986", {"start": v(-9.33, -17.7) * mm, "end": v(-9.22, -17.6) * mm});
            skLineSegment(sketch, "E987", {"start": v(-9.22, -17.6) * mm, "end": v(-9.11, -17.48) * mm});
            skLineSegment(sketch, "E988", {"start": v(-9.11, -17.48) * mm, "end": v(-9, -17.34) * mm});
            skLineSegment(sketch, "E989", {"start": v(-9, -17.34) * mm, "end": v(-8.8, -17.09) * mm});
            skLineSegment(sketch, "E990", {"start": v(-8.8, -17.09) * mm, "end": v(-8.78, -17.07) * mm});
            skLineSegment(sketch, "E991", {"start": v(-8.78, -17.07) * mm, "end": v(-8.06, -17.42) * mm});
            skLineSegment(sketch, "E992", {"start": v(-8.06, -17.42) * mm, "end": v(-8.07, -17.44) * mm});
            skLineSegment(sketch, "E993", {"start": v(-8.07, -17.44) * mm, "end": v(-8.15, -17.75) * mm});
            skLineSegment(sketch, "E994", {"start": v(-8.15, -17.75) * mm, "end": v(-8.18, -17.93) * mm});
            skLineSegment(sketch, "E995", {"start": v(-8.18, -17.93) * mm, "end": v(-8.2, -18.09) * mm});
            skLineSegment(sketch, "E996", {"start": v(-8.2, -18.09) * mm, "end": v(-8.23, -18.24) * mm});
            skLineSegment(sketch, "E997", {"start": v(-8.23, -18.24) * mm, "end": v(-8.24, -18.37) * mm});
            skLineSegment(sketch, "E998", {"start": v(-8.24, -18.37) * mm, "end": v(-8.25, -18.5) * mm});
            skLineSegment(sketch, "E999", {"start": v(-8.25, -18.5) * mm, "end": v(-8.26, -18.64) * mm});
            skLineSegment(sketch, "E1000", {"start": v(-8.26, -18.64) * mm, "end": v(-8.26, -18.76) * mm});
            skLineSegment(sketch, "E1001", {"start": v(-8.26, -18.76) * mm, "end": v(-8.27, -18.89) * mm});
            skLineSegment(sketch, "E1002", {"start": v(-8.27, -18.89) * mm, "end": v(-8.27, -19) * mm});
            skLineSegment(sketch, "E1003", {"start": v(-8.27, -19) * mm, "end": v(-8.27, -19.13) * mm});
            skLineSegment(sketch, "E1004", {"start": v(-8.27, -19.13) * mm, "end": v(-8.27, -19.25) * mm});
            skLineSegment(sketch, "E1005", {"start": v(-8.27, -19.25) * mm, "end": v(-8.26, -19.36) * mm});
            skLineSegment(sketch, "E1006", {"start": v(-8.26, -19.36) * mm, "end": v(-8.26, -19.48) * mm});
            skLineSegment(sketch, "E1007", {"start": v(-8.26, -19.48) * mm, "end": v(-7.62, -19.74) * mm});
            skLineSegment(sketch, "E1008", {"start": v(-7.62, -19.74) * mm, "end": v(-7.53, -19.66) * mm});
            skLineSegment(sketch, "E1009", {"start": v(-7.53, -19.66) * mm, "end": v(-7.45, -19.58) * mm});
            skLineSegment(sketch, "E1010", {"start": v(-7.45, -19.58) * mm, "end": v(-7.36, -19.5) * mm});
            skLineSegment(sketch, "E1011", {"start": v(-7.36, -19.5) * mm, "end": v(-7.28, -19.4) * mm});
            skLineSegment(sketch, "E1012", {"start": v(-7.28, -19.4) * mm, "end": v(-7.2, -19.32) * mm});
            skLineSegment(sketch, "E1013", {"start": v(-7.2, -19.32) * mm, "end": v(-7.11, -19.23) * mm});
            skLineSegment(sketch, "E1014", {"start": v(-7.11, -19.23) * mm, "end": v(-7.03, -19.13) * mm});
            skLineSegment(sketch, "E1015", {"start": v(-7.03, -19.13) * mm, "end": v(-6.95, -19.04) * mm});
            skLineSegment(sketch, "E1016", {"start": v(-6.95, -19.04) * mm, "end": v(-6.86, -18.93) * mm});
            skLineSegment(sketch, "E1017", {"start": v(-6.86, -18.93) * mm, "end": v(-6.77, -18.82) * mm});
            skLineSegment(sketch, "E1018", {"start": v(-6.77, -18.82) * mm, "end": v(-6.69, -18.7) * mm});
            skLineSegment(sketch, "E1019", {"start": v(-6.69, -18.7) * mm, "end": v(-6.6, -18.58) * mm});
            skLineSegment(sketch, "E1020", {"start": v(-6.6, -18.58) * mm, "end": v(-6.5, -18.42) * mm});
            skLineSegment(sketch, "E1021", {"start": v(-6.5, -18.42) * mm, "end": v(-6.33, -18.14) * mm});
            skLineSegment(sketch, "E1022", {"start": v(-6.33, -18.14) * mm, "end": v(-6.32, -18.12) * mm});
            skLineSegment(sketch, "E1023", {"start": v(-6.32, -18.12) * mm, "end": v(-5.56, -18.37) * mm});
            skLineSegment(sketch, "E1024", {"start": v(-5.56, -18.37) * mm, "end": v(-5.57, -18.39) * mm});
            skLineSegment(sketch, "E1025", {"start": v(-5.57, -18.39) * mm, "end": v(-5.6, -18.71) * mm});
            skLineSegment(sketch, "E1026", {"start": v(-5.6, -18.71) * mm, "end": v(-5.6, -18.9) * mm});
            skLineSegment(sketch, "E1027", {"start": v(-5.6, -18.9) * mm, "end": v(-5.61, -19.05) * mm});
            skLineSegment(sketch, "E1028", {"start": v(-5.61, -19.05) * mm, "end": v(-5.6, -19.2) * mm});
            skLineSegment(sketch, "E1029", {"start": v(-5.6, -19.2) * mm, "end": v(-5.6, -19.34) * mm});
            skLineSegment(sketch, "E1030", {"start": v(-5.6, -19.34) * mm, "end": v(-5.6, -19.47) * mm});
            skLineSegment(sketch, "E1031", {"start": v(-5.6, -19.47) * mm, "end": v(-5.58, -19.6) * mm});
            skLineSegment(sketch, "E1032", {"start": v(-5.58, -19.6) * mm, "end": v(-5.57, -19.73) * mm});
            skLineSegment(sketch, "E1033", {"start": v(-5.57, -19.73) * mm, "end": v(-5.56, -19.85) * mm});
            skLineSegment(sketch, "E1034", {"start": v(-5.56, -19.85) * mm, "end": v(-5.54, -19.97) * mm});
            skLineSegment(sketch, "E1035", {"start": v(-5.54, -19.97) * mm, "end": v(-5.52, -20.1) * mm});
            skLineSegment(sketch, "E1036", {"start": v(-5.52, -20.1) * mm, "end": v(-5.5, -20.2) * mm});
            skLineSegment(sketch, "E1037", {"start": v(-5.5, -20.2) * mm, "end": v(-5.49, -20.32) * mm});
            skLineSegment(sketch, "E1038", {"start": v(-5.49, -20.32) * mm, "end": v(-5.47, -20.44) * mm});
            skLineSegment(sketch, "E1039", {"start": v(-5.47, -20.44) * mm, "end": v(-4.8, -20.6) * mm});
            skLineSegment(sketch, "E1040", {"start": v(-4.8, -20.6) * mm, "end": v(-4.72, -20.51) * mm});
            skLineSegment(sketch, "E1041", {"start": v(-4.72, -20.51) * mm, "end": v(-4.65, -20.42) * mm});
            skLineSegment(sketch, "E1042", {"start": v(-4.65, -20.42) * mm, "end": v(-4.58, -20.33) * mm});
            skLineSegment(sketch, "E1043", {"start": v(-4.58, -20.33) * mm, "end": v(-4.5, -20.23) * mm});
            skLineSegment(sketch, "E1044", {"start": v(-4.5, -20.23) * mm, "end": v(-4.44, -20.13) * mm});
            skLineSegment(sketch, "E1045", {"start": v(-4.44, -20.13) * mm, "end": v(-4.37, -20.03) * mm});
            skLineSegment(sketch, "E1046", {"start": v(-4.37, -20.03) * mm, "end": v(-4.3, -19.92) * mm});
            skLineSegment(sketch, "E1047", {"start": v(-4.3, -19.92) * mm, "end": v(-4.23, -19.82) * mm});
            skLineSegment(sketch, "E1048", {"start": v(-4.23, -19.82) * mm, "end": v(-4.16, -19.7) * mm});
            skLineSegment(sketch, "E1049", {"start": v(-4.16, -19.7) * mm, "end": v(-4.09, -19.58) * mm});
            skLineSegment(sketch, "E1050", {"start": v(-4.09, -19.58) * mm, "end": v(-4.02, -19.45) * mm});
            skLineSegment(sketch, "E1051", {"start": v(-4.02, -19.45) * mm, "end": v(-3.94, -19.31) * mm});
            skLineSegment(sketch, "E1052", {"start": v(-3.94, -19.31) * mm, "end": v(-3.86, -19.15) * mm});
            skLineSegment(sketch, "E1053", {"start": v(-3.86, -19.15) * mm, "end": v(-3.74, -18.84) * mm});
            skLineSegment(sketch, "E1054", {"start": v(-3.74, -18.84) * mm, "end": v(-3.74, -18.82) * mm});
            skLineSegment(sketch, "E1055", {"start": v(-3.74, -18.82) * mm, "end": v(-2.95, -18.96) * mm});
            skLineSegment(sketch, "E1056", {"start": v(-2.95, -18.96) * mm, "end": v(-2.95, -18.98) * mm});
            skLineSegment(sketch, "E1057", {"start": v(-2.95, -18.98) * mm, "end": v(-2.94, -19.3) * mm});
            skLineSegment(sketch, "E1058", {"start": v(-2.94, -19.3) * mm, "end": v(-2.93, -19.49) * mm});
            skLineSegment(sketch, "E1059", {"start": v(-2.93, -19.49) * mm, "end": v(-2.9, -19.65) * mm});
            skLineSegment(sketch, "E1060", {"start": v(-2.9, -19.65) * mm, "end": v(-2.88, -19.8) * mm});
            skLineSegment(sketch, "E1061", {"start": v(-2.88, -19.8) * mm, "end": v(-2.86, -19.93) * mm});
            skLineSegment(sketch, "E1062", {"start": v(-2.86, -19.93) * mm, "end": v(-2.83, -20.06) * mm});
            skLineSegment(sketch, "E1063", {"start": v(-2.83, -20.06) * mm, "end": v(-2.8, -20.19) * mm});
            skLineSegment(sketch, "E1064", {"start": v(-2.8, -20.19) * mm, "end": v(-2.77, -20.31) * mm});
            skLineSegment(sketch, "E1065", {"start": v(-2.77, -20.31) * mm, "end": v(-2.74, -20.43) * mm});
            skLineSegment(sketch, "E1066", {"start": v(-2.74, -20.43) * mm, "end": v(-2.7, -20.55) * mm});
            skLineSegment(sketch, "E1067", {"start": v(-2.7, -20.55) * mm, "end": v(-2.68, -20.66) * mm});
            skLineSegment(sketch, "E1068", {"start": v(-2.68, -20.66) * mm, "end": v(-2.64, -20.78) * mm});
            skLineSegment(sketch, "E1069", {"start": v(-2.64, -20.78) * mm, "end": v(-2.6, -20.89) * mm});
            skLineSegment(sketch, "E1070", {"start": v(-2.6, -20.89) * mm, "end": v(-2.57, -21) * mm});
            skLineSegment(sketch, "E1071", {"start": v(-2.57, -21) * mm, "end": v(-1.88, -21.07) * mm});
            skLineSegment(sketch, "E1072", {"start": v(-1.88, -21.07) * mm, "end": v(-1.82, -20.97) * mm});
            skLineSegment(sketch, "E1073", {"start": v(-1.82, -20.97) * mm, "end": v(-1.76, -20.87) * mm});
            skLineSegment(sketch, "E1074", {"start": v(-1.76, -20.87) * mm, "end": v(-1.7, -20.76) * mm});
            skLineSegment(sketch, "E1075", {"start": v(-1.7, -20.76) * mm, "end": v(-1.65, -20.66) * mm});
            skLineSegment(sketch, "E1076", {"start": v(-1.65, -20.66) * mm, "end": v(-1.6, -20.55) * mm});
            skLineSegment(sketch, "E1077", {"start": v(-1.6, -20.55) * mm, "end": v(-1.54, -20.44) * mm});
            skLineSegment(sketch, "E1078", {"start": v(-1.54, -20.44) * mm, "end": v(-1.48, -20.33) * mm});
            skLineSegment(sketch, "E1079", {"start": v(-1.48, -20.33) * mm, "end": v(-1.43, -20.2) * mm});
            skLineSegment(sketch, "E1080", {"start": v(-1.43, -20.2) * mm, "end": v(-1.38, -20.09) * mm});
            skLineSegment(sketch, "E1081", {"start": v(-1.38, -20.09) * mm, "end": v(-1.32, -19.96) * mm});
            skLineSegment(sketch, "E1082", {"start": v(-1.32, -19.96) * mm, "end": v(-1.27, -19.82) * mm});
            skLineSegment(sketch, "E1083", {"start": v(-1.27, -19.82) * mm, "end": v(-1.22, -19.67) * mm});
            skLineSegment(sketch, "E1084", {"start": v(-1.22, -19.67) * mm, "end": v(-1.16, -19.5) * mm});
            skLineSegment(sketch, "E1085", {"start": v(-1.16, -19.5) * mm, "end": v(-1.08, -19.18) * mm});
            skLineSegment(sketch, "E1086", {"start": v(-1.08, -19.18) * mm, "end": v(-1.08, -19.16) * mm});
            skLineSegment(sketch, "E1087", {"start": v(-1.08, -19.16) * mm, "end": v(-0.28, -19.19) * mm});
            skLineSegment(sketch, "E1088", {"start": v(-0.28, -19.19) * mm, "end": v(-0.28, -19.2) * mm});
            skLineSegment(sketch, "E1089", {"start": v(-0.28, -19.2) * mm, "end": v(-0.23, -19.53) * mm});
            skLineSegment(sketch, "E1090", {"start": v(-0.23, -19.53) * mm, "end": v(-0.18, -19.7) * mm});
            skLineSegment(sketch, "E1091", {"start": v(-0.18, -19.7) * mm, "end": v(-0.14, -19.86) * mm});
            skLineSegment(sketch, "E1092", {"start": v(-0.14, -19.86) * mm, "end": v(-0.1, -20) * mm});
            skLineSegment(sketch, "E1093", {"start": v(-0.1, -20) * mm, "end": v(-0.06, -20.13) * mm});
            skLineSegment(sketch, "E1094", {"start": v(-0.06, -20.13) * mm, "end": v(-0.01, -20.26) * mm});
            skLineSegment(sketch, "E1095", {"start": v(-0.01, -20.26) * mm, "end": v(0.04, -20.38) * mm});
            skLineSegment(sketch, "E1096", {"start": v(0.04, -20.38) * mm, "end": v(0.08, -20.5) * mm});
            skLineSegment(sketch, "E1097", {"start": v(0.08, -20.5) * mm, "end": v(0.13, -20.61) * mm});
            skLineSegment(sketch, "E1098", {"start": v(0.13, -20.61) * mm, "end": v(0.18, -20.72) * mm});
            skLineSegment(sketch, "E1099", {"start": v(0.18, -20.72) * mm, "end": v(0.23, -20.83) * mm});
            skLineSegment(sketch, "E1100", {"start": v(0.23, -20.83) * mm, "end": v(0.28, -20.94) * mm});
            skLineSegment(sketch, "E1101", {"start": v(0.28, -20.94) * mm, "end": v(0.33, -21.04) * mm});
            skLineSegment(sketch, "E1102", {"start": v(0.33, -21.04) * mm, "end": v(0.38, -21.15) * mm});
            skLineSegment(sketch, "E1103", {"start": v(0.38, -21.15) * mm, "end": v(1.07, -21.12) * mm});
            skLineSegment(sketch, "E1104", {"start": v(1.07, -21.12) * mm, "end": v(1.11, -21.02) * mm});
            skLineSegment(sketch, "E1105", {"start": v(1.11, -21.02) * mm, "end": v(1.16, -20.9) * mm});
            skLineSegment(sketch, "E1106", {"start": v(1.16, -20.9) * mm, "end": v(1.2, -20.8) * mm});
            skLineSegment(sketch, "E1107", {"start": v(1.2, -20.8) * mm, "end": v(1.24, -20.69) * mm});
            skLineSegment(sketch, "E1108", {"start": v(1.24, -20.69) * mm, "end": v(1.28, -20.57) * mm});
            skLineSegment(sketch, "E1109", {"start": v(1.28, -20.57) * mm, "end": v(1.32, -20.45) * mm});
            skLineSegment(sketch, "E1110", {"start": v(1.32, -20.45) * mm, "end": v(1.36, -20.33) * mm});
            skLineSegment(sketch, "E1111", {"start": v(1.36, -20.33) * mm, "end": v(1.4, -20.2) * mm});
            skLineSegment(sketch, "E1112", {"start": v(1.4, -20.2) * mm, "end": v(1.43, -20.08) * mm});
            skLineSegment(sketch, "E1113", {"start": v(1.43, -20.08) * mm, "end": v(1.47, -19.95) * mm});
            skLineSegment(sketch, "E1114", {"start": v(1.47, -19.95) * mm, "end": v(1.5, -19.8) * mm});
            skLineSegment(sketch, "E1115", {"start": v(1.5, -19.8) * mm, "end": v(1.53, -19.65) * mm});
            skLineSegment(sketch, "E1116", {"start": v(1.53, -19.65) * mm, "end": v(1.56, -19.46) * mm});
            skLineSegment(sketch, "E1117", {"start": v(1.56, -19.46) * mm, "end": v(1.6, -19.14) * mm});
            skLineSegment(sketch, "E1118", {"start": v(1.6, -19.14) * mm, "end": v(1.6, -19.12) * mm});
            skLineSegment(sketch, "E1119", {"start": v(1.6, -19.12) * mm, "end": v(2.39, -19.04) * mm});
            skLineSegment(sketch, "E1120", {"start": v(2.39, -19.04) * mm, "end": v(2.4, -19.06) * mm});
            skLineSegment(sketch, "E1121", {"start": v(2.4, -19.06) * mm, "end": v(2.5, -19.37) * mm});
            skLineSegment(sketch, "E1122", {"start": v(2.5, -19.37) * mm, "end": v(2.56, -19.54) * mm});
            skLineSegment(sketch, "E1123", {"start": v(2.56, -19.54) * mm, "end": v(2.62, -19.68) * mm});
            skLineSegment(sketch, "E1124", {"start": v(2.62, -19.68) * mm, "end": v(2.69, -19.82) * mm});
            skLineSegment(sketch, "E1125", {"start": v(2.69, -19.82) * mm, "end": v(2.75, -19.94) * mm});
            skLineSegment(sketch, "E1126", {"start": v(2.75, -19.94) * mm, "end": v(2.8, -20.06) * mm});
            skLineSegment(sketch, "E1127", {"start": v(2.8, -20.06) * mm, "end": v(2.87, -20.17) * mm});
            skLineSegment(sketch, "E1128", {"start": v(2.87, -20.17) * mm, "end": v(2.93, -20.28) * mm});
            skLineSegment(sketch, "E1129", {"start": v(2.93, -20.28) * mm, "end": v(3, -20.4) * mm});
            skLineSegment(sketch, "E1130", {"start": v(3, -20.4) * mm, "end": v(3.06, -20.5) * mm});
            skLineSegment(sketch, "E1131", {"start": v(3.06, -20.5) * mm, "end": v(3.12, -20.6) * mm});
            skLineSegment(sketch, "E1132", {"start": v(3.12, -20.6) * mm, "end": v(3.19, -20.7) * mm});
            skLineSegment(sketch, "E1133", {"start": v(3.19, -20.7) * mm, "end": v(3.25, -20.8) * mm});
            skLineSegment(sketch, "E1134", {"start": v(3.25, -20.8) * mm, "end": v(3.32, -20.89) * mm});
            skLineSegment(sketch, "E1135", {"start": v(3.32, -20.89) * mm, "end": v(4, -20.77) * mm});
            skLineSegment(sketch, "E1136", {"start": v(4, -20.77) * mm, "end": v(4.03, -20.65) * mm});
            skLineSegment(sketch, "E1137", {"start": v(4.03, -20.65) * mm, "end": v(4.06, -20.54) * mm});
            skLineSegment(sketch, "E1138", {"start": v(4.06, -20.54) * mm, "end": v(4.08, -20.43) * mm});
            skLineSegment(sketch, "E1139", {"start": v(4.08, -20.43) * mm, "end": v(4.1, -20.31) * mm});
            skLineSegment(sketch, "E1140", {"start": v(4.1, -20.31) * mm, "end": v(4.13, -20.2) * mm});
            skLineSegment(sketch, "E1141", {"start": v(4.13, -20.2) * mm, "end": v(4.15, -20.07) * mm});
            skLineSegment(sketch, "E1142", {"start": v(4.15, -20.07) * mm, "end": v(4.18, -19.94) * mm});
            skLineSegment(sketch, "E1143", {"start": v(4.18, -19.94) * mm, "end": v(4.2, -19.82) * mm});
            skLineSegment(sketch, "E1144", {"start": v(4.2, -19.82) * mm, "end": v(4.21, -19.68) * mm});
            skLineSegment(sketch, "E1145", {"start": v(4.21, -19.68) * mm, "end": v(4.23, -19.54) * mm});
            skLineSegment(sketch, "E1146", {"start": v(4.23, -19.54) * mm, "end": v(4.24, -19.4) * mm});
            skLineSegment(sketch, "E1147", {"start": v(4.24, -19.4) * mm, "end": v(4.25, -19.24) * mm});
            skLineSegment(sketch, "E1148", {"start": v(4.25, -19.24) * mm, "end": v(4.26, -19.06) * mm});
            skLineSegment(sketch, "E1149", {"start": v(4.26, -19.06) * mm, "end": v(4.24, -18.73) * mm});
            skLineSegment(sketch, "E1150", {"start": v(4.24, -18.73) * mm, "end": v(4.24, -18.71) * mm});
            skLineSegment(sketch, "E1151", {"start": v(4.24, -18.71) * mm, "end": v(5.02, -18.52) * mm});
            skLineSegment(sketch, "E1152", {"start": v(5.02, -18.52) * mm, "end": v(5.02, -18.54) * mm});
            skLineSegment(sketch, "E1153", {"start": v(5.02, -18.54) * mm, "end": v(5.16, -18.83) * mm});
            skLineSegment(sketch, "E1154", {"start": v(5.16, -18.83) * mm, "end": v(5.25, -18.99) * mm});
            skLineSegment(sketch, "E1155", {"start": v(5.25, -18.99) * mm, "end": v(5.34, -19.13) * mm});
            skLineSegment(sketch, "E1156", {"start": v(5.34, -19.13) * mm, "end": v(5.42, -19.25) * mm});
            skLineSegment(sketch, "E1157", {"start": v(5.42, -19.25) * mm, "end": v(5.5, -19.36) * mm});
            skLineSegment(sketch, "E1158", {"start": v(5.5, -19.36) * mm, "end": v(5.57, -19.47) * mm});
            skLineSegment(sketch, "E1159", {"start": v(5.57, -19.47) * mm, "end": v(5.65, -19.58) * mm});
            skLineSegment(sketch, "E1160", {"start": v(5.65, -19.58) * mm, "end": v(5.73, -19.68) * mm});
            skLineSegment(sketch, "E1161", {"start": v(5.73, -19.68) * mm, "end": v(5.8, -19.77) * mm});
            skLineSegment(sketch, "E1162", {"start": v(5.8, -19.77) * mm, "end": v(5.88, -19.87) * mm});
            skLineSegment(sketch, "E1163", {"start": v(5.88, -19.87) * mm, "end": v(5.96, -19.96) * mm});
            skLineSegment(sketch, "E1164", {"start": v(5.96, -19.96) * mm, "end": v(6.04, -20.05) * mm});
            skLineSegment(sketch, "E1165", {"start": v(6.04, -20.05) * mm, "end": v(6.11, -20.13) * mm});
            skLineSegment(sketch, "E1166", {"start": v(6.11, -20.13) * mm, "end": v(6.2, -20.22) * mm});
            skLineSegment(sketch, "E1167", {"start": v(6.2, -20.22) * mm, "end": v(6.85, -20) * mm});
            skLineSegment(sketch, "E1168", {"start": v(6.85, -20) * mm, "end": v(6.86, -19.9) * mm});
            skLineSegment(sketch, "E1169", {"start": v(6.86, -19.9) * mm, "end": v(6.88, -19.78) * mm});
            skLineSegment(sketch, "E1170", {"start": v(6.88, -19.78) * mm, "end": v(6.89, -19.66) * mm});
            skLineSegment(sketch, "E1171", {"start": v(6.89, -19.66) * mm, "end": v(6.9, -19.54) * mm});
            skLineSegment(sketch, "E1172", {"start": v(6.9, -19.54) * mm, "end": v(6.9, -19.42) * mm});
            skLineSegment(sketch, "E1173", {"start": v(6.9, -19.42) * mm, "end": v(6.9, -19.3) * mm});
            skLineSegment(sketch, "E1174", {"start": v(6.9, -19.3) * mm, "end": v(6.91, -19.17) * mm});
            skLineSegment(sketch, "E1175", {"start": v(6.91, -19.17) * mm, "end": v(6.91, -19.04) * mm});
            skLineSegment(sketch, "E1176", {"start": v(6.91, -19.04) * mm, "end": v(6.91, -18.9) * mm});
            skLineSegment(sketch, "E1177", {"start": v(6.91, -18.9) * mm, "end": v(6.9, -18.76) * mm});
            skLineSegment(sketch, "E1178", {"start": v(6.9, -18.76) * mm, "end": v(6.9, -18.62) * mm});
            skLineSegment(sketch, "E1179", {"start": v(6.9, -18.62) * mm, "end": v(6.89, -18.46) * mm});
            skLineSegment(sketch, "E1180", {"start": v(6.89, -18.46) * mm, "end": v(6.87, -18.28) * mm});
            skLineSegment(sketch, "E1181", {"start": v(6.87, -18.28) * mm, "end": v(6.8, -17.96) * mm});
            skLineSegment(sketch, "E1182", {"start": v(6.8, -17.96) * mm, "end": v(6.8, -17.94) * mm});
            skLineSegment(sketch, "E1183", {"start": v(6.8, -17.94) * mm, "end": v(7.54, -17.64) * mm});
            skLineSegment(sketch, "E1184", {"start": v(7.54, -17.64) * mm, "end": v(7.55, -17.66) * mm});
            skLineSegment(sketch, "E1185", {"start": v(7.55, -17.66) * mm, "end": v(7.73, -17.93) * mm});
            skLineSegment(sketch, "E1186", {"start": v(7.73, -17.93) * mm, "end": v(7.85, -18.07) * mm});
            skLineSegment(sketch, "E1187", {"start": v(7.85, -18.07) * mm, "end": v(7.95, -18.2) * mm});
            skLineSegment(sketch, "E1188", {"start": v(7.95, -18.2) * mm, "end": v(8.04, -18.3) * mm});
            skLineSegment(sketch, "E1189", {"start": v(8.04, -18.3) * mm, "end": v(8.14, -18.4) * mm});
            skLineSegment(sketch, "E1190", {"start": v(8.14, -18.4) * mm, "end": v(8.23, -18.5) * mm});
            skLineSegment(sketch, "E1191", {"start": v(8.23, -18.5) * mm, "end": v(8.32, -18.6) * mm});
            skLineSegment(sketch, "E1192", {"start": v(8.32, -18.6) * mm, "end": v(8.41, -18.69) * mm});
            skLineSegment(sketch, "E1193", {"start": v(8.41, -18.69) * mm, "end": v(8.5, -18.77) * mm});
            skLineSegment(sketch, "E1194", {"start": v(8.5, -18.77) * mm, "end": v(8.59, -18.85) * mm});
            skLineSegment(sketch, "E1195", {"start": v(8.59, -18.85) * mm, "end": v(8.68, -18.93) * mm});
            skLineSegment(sketch, "E1196", {"start": v(8.68, -18.93) * mm, "end": v(8.77, -19.01) * mm});
            skLineSegment(sketch, "E1197", {"start": v(8.77, -19.01) * mm, "end": v(8.86, -19.09) * mm});
            skLineSegment(sketch, "E1198", {"start": v(8.86, -19.09) * mm, "end": v(8.95, -19.16) * mm});
            skLineSegment(sketch, "E1199", {"start": v(8.95, -19.16) * mm, "end": v(9.57, -18.86) * mm});
            skLineSegment(sketch, "E1200", {"start": v(9.57, -18.86) * mm, "end": v(9.56, -18.74) * mm});
            skLineSegment(sketch, "E1201", {"start": v(9.56, -18.74) * mm, "end": v(9.56, -18.62) * mm});
            skLineSegment(sketch, "E1202", {"start": v(9.56, -18.62) * mm, "end": v(9.55, -18.5) * mm});
            skLineSegment(sketch, "E1203", {"start": v(9.55, -18.5) * mm, "end": v(9.55, -18.39) * mm});
            skLineSegment(sketch, "E1204", {"start": v(9.55, -18.39) * mm, "end": v(9.54, -18.27) * mm});
            skLineSegment(sketch, "E1205", {"start": v(9.54, -18.27) * mm, "end": v(9.53, -18.14) * mm});
            skLineSegment(sketch, "E1206", {"start": v(9.53, -18.14) * mm, "end": v(9.51, -18.02) * mm});
            skLineSegment(sketch, "E1207", {"start": v(9.51, -18.02) * mm, "end": v(9.5, -17.89) * mm});
            skLineSegment(sketch, "E1208", {"start": v(9.5, -17.89) * mm, "end": v(9.47, -17.76) * mm});
            skLineSegment(sketch, "E1209", {"start": v(9.47, -17.76) * mm, "end": v(9.45, -17.62) * mm});
            skLineSegment(sketch, "E1210", {"start": v(9.45, -17.62) * mm, "end": v(9.42, -17.47) * mm});
            skLineSegment(sketch, "E1211", {"start": v(9.42, -17.47) * mm, "end": v(9.39, -17.32) * mm});
            skLineSegment(sketch, "E1212", {"start": v(9.39, -17.32) * mm, "end": v(9.34, -17.14) * mm});
            skLineSegment(sketch, "E1213", {"start": v(9.34, -17.14) * mm, "end": v(9.24, -16.83) * mm});
            skLineSegment(sketch, "E1214", {"start": v(9.24, -16.83) * mm, "end": v(9.23, -16.82) * mm});
            skLineSegment(sketch, "E1215", {"start": v(9.23, -16.82) * mm, "end": v(9.93, -16.41) * mm});
            skLineSegment(sketch, "E1216", {"start": v(9.93, -16.41) * mm, "end": v(9.94, -16.43) * mm});
            skLineSegment(sketch, "E1217", {"start": v(9.94, -16.43) * mm, "end": v(10.15, -16.67) * mm});
            skLineSegment(sketch, "E1218", {"start": v(10.15, -16.67) * mm, "end": v(10.28, -16.8) * mm});
            skLineSegment(sketch, "E1219", {"start": v(10.28, -16.8) * mm, "end": v(10.4, -16.9) * mm});
            skLineSegment(sketch, "E1220", {"start": v(10.4, -16.9) * mm, "end": v(10.51, -17) * mm});
            skLineSegment(sketch, "E1221", {"start": v(10.51, -17) * mm, "end": v(10.62, -17.1) * mm});
            skLineSegment(sketch, "E1222", {"start": v(10.62, -17.1) * mm, "end": v(10.72, -17.18) * mm});
            skLineSegment(sketch, "E1223", {"start": v(10.72, -17.18) * mm, "end": v(10.83, -17.26) * mm});
            skLineSegment(sketch, "E1224", {"start": v(10.83, -17.26) * mm, "end": v(10.93, -17.33) * mm});
            skLineSegment(sketch, "E1225", {"start": v(10.93, -17.33) * mm, "end": v(11.03, -17.4) * mm});
            skLineSegment(sketch, "E1226", {"start": v(11.03, -17.4) * mm, "end": v(11.13, -17.47) * mm});
            skLineSegment(sketch, "E1227", {"start": v(11.13, -17.47) * mm, "end": v(11.23, -17.54) * mm});
            skLineSegment(sketch, "E1228", {"start": v(11.23, -17.54) * mm, "end": v(11.33, -17.6) * mm});
            skLineSegment(sketch, "E1229", {"start": v(11.33, -17.6) * mm, "end": v(11.43, -17.67) * mm});
            skLineSegment(sketch, "E1230", {"start": v(11.43, -17.67) * mm, "end": v(11.53, -17.73) * mm});
            skLineSegment(sketch, "E1231", {"start": v(11.53, -17.73) * mm, "end": v(12.1, -17.34) * mm});
            skLineSegment(sketch, "E1232", {"start": v(12.1, -17.34) * mm, "end": v(12.08, -17.23) * mm});
            skLineSegment(sketch, "E1233", {"start": v(12.08, -17.23) * mm, "end": v(12.06, -17.11) * mm});
            skLineSegment(sketch, "E1234", {"start": v(12.06, -17.11) * mm, "end": v(12.04, -17) * mm});
            skLineSegment(sketch, "E1235", {"start": v(12.04, -17) * mm, "end": v(12.01, -16.88) * mm});
            skLineSegment(sketch, "E1236", {"start": v(12.01, -16.88) * mm, "end": v(11.99, -16.76) * mm});
            skLineSegment(sketch, "E1237", {"start": v(11.99, -16.76) * mm, "end": v(11.96, -16.64) * mm});
            skLineSegment(sketch, "E1238", {"start": v(11.96, -16.64) * mm, "end": v(11.93, -16.52) * mm});
            skLineSegment(sketch, "E1239", {"start": v(11.93, -16.52) * mm, "end": v(11.9, -16.4) * mm});
            skLineSegment(sketch, "E1240", {"start": v(11.9, -16.4) * mm, "end": v(11.85, -16.26) * mm});
            skLineSegment(sketch, "E1241", {"start": v(11.85, -16.26) * mm, "end": v(11.81, -16.13) * mm});
            skLineSegment(sketch, "E1242", {"start": v(11.81, -16.13) * mm, "end": v(11.76, -16) * mm});
            skLineSegment(sketch, "E1243", {"start": v(11.76, -16) * mm, "end": v(11.7, -15.84) * mm});
            skLineSegment(sketch, "E1244", {"start": v(11.7, -15.84) * mm, "end": v(11.64, -15.67) * mm});
            skLineSegment(sketch, "E1245", {"start": v(11.64, -15.67) * mm, "end": v(11.5, -15.38) * mm});
            skLineSegment(sketch, "E1246", {"start": v(11.5, -15.38) * mm, "end": v(11.48, -15.36) * mm});
            skLineSegment(sketch, "E1247", {"start": v(11.48, -15.36) * mm, "end": v(12.11, -14.87) * mm});
            skLineSegment(sketch, "E1248", {"start": v(12.11, -14.87) * mm, "end": v(12.13, -14.89) * mm});
            skLineSegment(sketch, "E1249", {"start": v(12.13, -14.89) * mm, "end": v(12.37, -15.1) * mm});
            skLineSegment(sketch, "E1250", {"start": v(12.37, -15.1) * mm, "end": v(12.52, -15.2) * mm});
            skLineSegment(sketch, "E1251", {"start": v(12.52, -15.2) * mm, "end": v(12.65, -15.3) * mm});
            skLineSegment(sketch, "E1252", {"start": v(12.65, -15.3) * mm, "end": v(12.78, -15.38) * mm});
            skLineSegment(sketch, "E1253", {"start": v(12.78, -15.38) * mm, "end": v(12.9, -15.45) * mm});
            skLineSegment(sketch, "E1254", {"start": v(12.9, -15.45) * mm, "end": v(13.01, -15.52) * mm});
            skLineSegment(sketch, "E1255", {"start": v(13.01, -15.52) * mm, "end": v(13.12, -15.58) * mm});
            skLineSegment(sketch, "E1256", {"start": v(13.12, -15.58) * mm, "end": v(13.23, -15.64) * mm});
            skLineSegment(sketch, "E1257", {"start": v(13.23, -15.64) * mm, "end": v(13.34, -15.7) * mm});
            skLineSegment(sketch, "E1258", {"start": v(13.34, -15.7) * mm, "end": v(13.45, -15.75) * mm});
            skLineSegment(sketch, "E1259", {"start": v(13.45, -15.75) * mm, "end": v(13.56, -15.8) * mm});
            skLineSegment(sketch, "E1260", {"start": v(13.56, -15.8) * mm, "end": v(13.67, -15.85) * mm});
            skLineSegment(sketch, "E1261", {"start": v(13.67, -15.85) * mm, "end": v(13.77, -15.9) * mm});
            skLineSegment(sketch, "E1262", {"start": v(13.77, -15.9) * mm, "end": v(13.88, -15.95) * mm});
            skLineSegment(sketch, "E1263", {"start": v(13.88, -15.95) * mm, "end": v(14.4, -15.48) * mm});
            skLineSegment(sketch, "E1264", {"start": v(14.4, -15.48) * mm, "end": v(14.36, -15.37) * mm});
            skLineSegment(sketch, "E1265", {"start": v(14.36, -15.37) * mm, "end": v(14.32, -15.26) * mm});
            skLineSegment(sketch, "E1266", {"start": v(14.32, -15.26) * mm, "end": v(14.28, -15.15) * mm});
            skLineSegment(sketch, "E1267", {"start": v(14.28, -15.15) * mm, "end": v(14.24, -15.04) * mm});
            skLineSegment(sketch, "E1268", {"start": v(14.24, -15.04) * mm, "end": v(14.2, -14.93) * mm});
            skLineSegment(sketch, "E1269", {"start": v(14.2, -14.93) * mm, "end": v(14.16, -14.81) * mm});
            skLineSegment(sketch, "E1270", {"start": v(14.16, -14.81) * mm, "end": v(14.1, -14.7) * mm});
            skLineSegment(sketch, "E1271", {"start": v(14.1, -14.7) * mm, "end": v(14.06, -14.57) * mm});
            skLineSegment(sketch, "E1272", {"start": v(14.06, -14.57) * mm, "end": v(14, -14.45) * mm});
            skLineSegment(sketch, "E1273", {"start": v(14, -14.45) * mm, "end": v(13.94, -14.33) * mm});
            skLineSegment(sketch, "E1274", {"start": v(13.94, -14.33) * mm, "end": v(13.87, -14.2) * mm});
            skLineSegment(sketch, "E1275", {"start": v(13.87, -14.2) * mm, "end": v(13.8, -14.06) * mm});
            skLineSegment(sketch, "E1276", {"start": v(13.8, -14.06) * mm, "end": v(13.7, -13.9) * mm});
            skLineSegment(sketch, "E1277", {"start": v(13.7, -13.9) * mm, "end": v(13.52, -13.63) * mm});
            skLineSegment(sketch, "E1278", {"start": v(13.52, -13.63) * mm, "end": v(13.5, -13.62) * mm});
            skLineSegment(sketch, "E1279", {"start": v(13.5, -13.62) * mm, "end": v(14.07, -13.04) * mm});
            skLineSegment(sketch, "E1280", {"start": v(14.07, -13.04) * mm, "end": v(14.08, -13.05) * mm});
            skLineSegment(sketch, "E1281", {"start": v(14.08, -13.05) * mm, "end": v(14.36, -13.23) * mm});
            skLineSegment(sketch, "E1282", {"start": v(14.36, -13.23) * mm, "end": v(14.52, -13.31) * mm});
            skLineSegment(sketch, "E1283", {"start": v(14.52, -13.31) * mm, "end": v(14.66, -13.38) * mm});
            skLineSegment(sketch, "E1284", {"start": v(14.66, -13.38) * mm, "end": v(14.8, -13.45) * mm});
            skLineSegment(sketch, "E1285", {"start": v(14.8, -13.45) * mm, "end": v(14.92, -13.5) * mm});
            skLineSegment(sketch, "E1286", {"start": v(14.92, -13.5) * mm, "end": v(15.04, -13.55) * mm});
            skLineSegment(sketch, "E1287", {"start": v(15.04, -13.55) * mm, "end": v(15.16, -13.6) * mm});
            skLineSegment(sketch, "E1288", {"start": v(15.16, -13.6) * mm, "end": v(15.28, -13.64) * mm});
            skLineSegment(sketch, "E1289", {"start": v(15.28, -13.64) * mm, "end": v(15.4, -13.69) * mm});
            skLineSegment(sketch, "E1290", {"start": v(15.4, -13.69) * mm, "end": v(15.51, -13.72) * mm});
            skLineSegment(sketch, "E1291", {"start": v(15.51, -13.72) * mm, "end": v(15.63, -13.76) * mm});
            skLineSegment(sketch, "E1292", {"start": v(15.63, -13.76) * mm, "end": v(15.74, -13.8) * mm});
            skLineSegment(sketch, "E1293", {"start": v(15.74, -13.8) * mm, "end": v(15.85, -13.83) * mm});
            skLineSegment(sketch, "E1294", {"start": v(15.85, -13.83) * mm, "end": v(15.96, -13.86) * mm});
            skLineSegment(sketch, "E1295", {"start": v(15.96, -13.86) * mm, "end": v(16.4, -13.33) * mm});
            skLineSegment(sketch, "E1296", {"start": v(16.4, -13.33) * mm, "end": v(16.36, -13.22) * mm});
            skLineSegment(sketch, "E1297", {"start": v(16.36, -13.22) * mm, "end": v(16.3, -13.12) * mm});
            skLineSegment(sketch, "E1298", {"start": v(16.3, -13.12) * mm, "end": v(16.25, -13.01) * mm});
            skLineSegment(sketch, "E1299", {"start": v(16.25, -13.01) * mm, "end": v(16.2, -12.9) * mm});
            skLineSegment(sketch, "E1300", {"start": v(16.2, -12.9) * mm, "end": v(16.14, -12.8) * mm});
            skLineSegment(sketch, "E1301", {"start": v(16.14, -12.8) * mm, "end": v(16.08, -12.7) * mm});
            skLineSegment(sketch, "E1302", {"start": v(16.08, -12.7) * mm, "end": v(16.02, -12.59) * mm});
            skLineSegment(sketch, "E1303", {"start": v(16.02, -12.59) * mm, "end": v(15.95, -12.47) * mm});
            skLineSegment(sketch, "E1304", {"start": v(15.95, -12.47) * mm, "end": v(15.88, -12.36) * mm});
            skLineSegment(sketch, "E1305", {"start": v(15.88, -12.36) * mm, "end": v(15.8, -12.25) * mm});
            skLineSegment(sketch, "E1306", {"start": v(15.8, -12.25) * mm, "end": v(15.71, -12.13) * mm});
            skLineSegment(sketch, "E1307", {"start": v(15.71, -12.13) * mm, "end": v(15.62, -12) * mm});
            skLineSegment(sketch, "E1308", {"start": v(15.62, -12) * mm, "end": v(15.5, -11.85) * mm});
            skLineSegment(sketch, "E1309", {"start": v(15.5, -11.85) * mm, "end": v(15.29, -11.61) * mm});
            skLineSegment(sketch, "E1310", {"start": v(15.29, -11.61) * mm, "end": v(15.27, -11.6) * mm});
            skLineSegment(sketch, "E1311", {"start": v(15.27, -11.6) * mm, "end": v(15.74, -10.95) * mm});
            skLineSegment(sketch, "E1312", {"start": v(15.74, -10.95) * mm, "end": v(15.76, -10.96) * mm});
            skLineSegment(sketch, "E1313", {"start": v(15.76, -10.96) * mm, "end": v(16.06, -11.1) * mm});
            skLineSegment(sketch, "E1314", {"start": v(16.06, -11.1) * mm, "end": v(16.23, -11.16) * mm});
            skLineSegment(sketch, "E1315", {"start": v(16.23, -11.16) * mm, "end": v(16.38, -11.21) * mm});
            skLineSegment(sketch, "E1316", {"start": v(16.38, -11.21) * mm, "end": v(16.52, -11.25) * mm});
            skLineSegment(sketch, "E1317", {"start": v(16.52, -11.25) * mm, "end": v(16.65, -11.3) * mm});
            skLineSegment(sketch, "E1318", {"start": v(16.65, -11.3) * mm, "end": v(16.78, -11.33) * mm});
            skLineSegment(sketch, "E1319", {"start": v(16.78, -11.33) * mm, "end": v(16.9, -11.36) * mm});
            skLineSegment(sketch, "E1320", {"start": v(16.9, -11.36) * mm, "end": v(17.03, -11.38) * mm});
            skLineSegment(sketch, "E1321", {"start": v(17.03, -11.38) * mm, "end": v(17.15, -11.4) * mm});
            skLineSegment(sketch, "E1322", {"start": v(17.15, -11.4) * mm, "end": v(17.27, -11.43) * mm});
            skLineSegment(sketch, "E1323", {"start": v(17.27, -11.43) * mm, "end": v(17.4, -11.45) * mm});
            skLineSegment(sketch, "E1324", {"start": v(17.4, -11.45) * mm, "end": v(17.5, -11.47) * mm});
            skLineSegment(sketch, "E1325", {"start": v(17.5, -11.47) * mm, "end": v(17.62, -11.48) * mm});
            skLineSegment(sketch, "E1326", {"start": v(17.62, -11.48) * mm, "end": v(17.74, -11.5) * mm});
            skLineSegment(sketch, "E1327", {"start": v(17.74, -11.5) * mm, "end": v(18.1, -10.91) * mm});
            skLineSegment(sketch, "E1328", {"start": v(18.1, -10.91) * mm, "end": v(18.04, -10.82) * mm});
            skLineSegment(sketch, "E1329", {"start": v(18.04, -10.82) * mm, "end": v(17.97, -10.72) * mm});
            skLineSegment(sketch, "E1330", {"start": v(17.97, -10.72) * mm, "end": v(17.9, -10.62) * mm});
            skLineSegment(sketch, "E1331", {"start": v(17.9, -10.62) * mm, "end": v(17.84, -10.53) * mm});
            skLineSegment(sketch, "E1332", {"start": v(17.84, -10.53) * mm, "end": v(17.77, -10.43) * mm});
            skLineSegment(sketch, "E1333", {"start": v(17.77, -10.43) * mm, "end": v(17.69, -10.33) * mm});
            skLineSegment(sketch, "E1334", {"start": v(17.69, -10.33) * mm, "end": v(17.61, -10.23) * mm});
            skLineSegment(sketch, "E1335", {"start": v(17.61, -10.23) * mm, "end": v(17.53, -10.13) * mm});
            skLineSegment(sketch, "E1336", {"start": v(17.53, -10.13) * mm, "end": v(17.44, -10.03) * mm});
            skLineSegment(sketch, "E1337", {"start": v(17.44, -10.03) * mm, "end": v(17.35, -9.93) * mm});
            skLineSegment(sketch, "E1338", {"start": v(17.35, -9.93) * mm, "end": v(17.25, -9.82) * mm});
            skLineSegment(sketch, "E1339", {"start": v(17.25, -9.82) * mm, "end": v(17.14, -9.7) * mm});
            skLineSegment(sketch, "E1340", {"start": v(17.14, -9.7) * mm, "end": v(17, -9.58) * mm});
            skLineSegment(sketch, "E1341", {"start": v(17, -9.58) * mm, "end": v(16.75, -9.37) * mm});
            skLineSegment(sketch, "E1342", {"start": v(16.75, -9.37) * mm, "end": v(16.74, -9.36) * mm});
            skLineSegment(sketch, "E1343", {"start": v(16.74, -9.36) * mm, "end": v(17.11, -8.65) * mm});
            skLineSegment(sketch, "E1344", {"start": v(17.11, -8.65) * mm, "end": v(17.13, -8.66) * mm});
            skLineSegment(sketch, "E1345", {"start": v(17.13, -8.66) * mm, "end": v(17.44, -8.75) * mm});
            skLineSegment(sketch, "E1346", {"start": v(17.44, -8.75) * mm, "end": v(17.62, -8.8) * mm});
            skLineSegment(sketch, "E1347", {"start": v(17.62, -8.8) * mm, "end": v(17.78, -8.82) * mm});
            skLineSegment(sketch, "E1348", {"start": v(17.78, -8.82) * mm, "end": v(17.92, -8.84) * mm});
            skLineSegment(sketch, "E1349", {"start": v(17.92, -8.84) * mm, "end": v(18.06, -8.86) * mm});
            skLineSegment(sketch, "E1350", {"start": v(18.06, -8.86) * mm, "end": v(18.2, -8.88) * mm});
            skLineSegment(sketch, "E1351", {"start": v(18.2, -8.88) * mm, "end": v(18.32, -8.9) * mm});
            skLineSegment(sketch, "E1352", {"start": v(18.32, -8.9) * mm, "end": v(18.45, -8.9) * mm});
            skLineSegment(sketch, "E1353", {"start": v(18.45, -8.9) * mm, "end": v(18.57, -8.9) * mm});
            skLineSegment(sketch, "E1354", {"start": v(18.57, -8.9) * mm, "end": v(18.7, -8.91) * mm});
            skLineSegment(sketch, "E1355", {"start": v(18.7, -8.91) * mm, "end": v(18.82, -8.92) * mm});
            skLineSegment(sketch, "E1356", {"start": v(18.82, -8.92) * mm, "end": v(18.93, -8.92) * mm});
            skLineSegment(sketch, "E1357", {"start": v(18.93, -8.92) * mm, "end": v(19.05, -8.92) * mm});
            skLineSegment(sketch, "E1358", {"start": v(19.05, -8.92) * mm, "end": v(19.16, -8.92) * mm});
            skLineSegment(sketch, "E1359", {"start": v(19.16, -8.92) * mm, "end": v(19.45, -8.29) * mm});
            skLineSegment(sketch, "E1360", {"start": v(19.45, -8.29) * mm, "end": v(19.37, -8.2) * mm});
            skLineSegment(sketch, "E1361", {"start": v(19.37, -8.2) * mm, "end": v(19.3, -8.11) * mm});
            skLineSegment(sketch, "E1362", {"start": v(19.3, -8.11) * mm, "end": v(19.21, -8.03) * mm});
            skLineSegment(sketch, "E1363", {"start": v(19.21, -8.03) * mm, "end": v(19.13, -7.94) * mm});
            skLineSegment(sketch, "E1364", {"start": v(19.13, -7.94) * mm, "end": v(19.04, -7.85) * mm});
            skLineSegment(sketch, "E1365", {"start": v(19.04, -7.85) * mm, "end": v(18.96, -7.77) * mm});
            skLineSegment(sketch, "E1366", {"start": v(18.96, -7.77) * mm, "end": v(18.86, -7.68) * mm});
            skLineSegment(sketch, "E1367", {"start": v(18.86, -7.68) * mm, "end": v(18.77, -7.6) * mm});
            skLineSegment(sketch, "E1368", {"start": v(18.77, -7.6) * mm, "end": v(18.67, -7.5) * mm});
            skLineSegment(sketch, "E1369", {"start": v(18.67, -7.5) * mm, "end": v(18.56, -7.41) * mm});
            skLineSegment(sketch, "E1370", {"start": v(18.56, -7.41) * mm, "end": v(18.45, -7.32) * mm});
            skLineSegment(sketch, "E1371", {"start": v(18.45, -7.32) * mm, "end": v(18.32, -7.22) * mm});
            skLineSegment(sketch, "E1372", {"start": v(18.32, -7.22) * mm, "end": v(18.17, -7.12) * mm});
            skLineSegment(sketch, "E1373", {"start": v(18.17, -7.12) * mm, "end": v(17.9, -6.94) * mm});
            skLineSegment(sketch, "E1374", {"start": v(17.9, -6.94) * mm, "end": v(17.88, -6.94) * mm});
            skLineSegment(sketch, "E1375", {"start": v(17.88, -6.94) * mm, "end": v(18.15, -6.19) * mm});
            skLineSegment(sketch, "E1376", {"start": v(18.15, -6.19) * mm, "end": v(18.17, -6.2) * mm});
            skLineSegment(sketch, "E1377", {"start": v(18.17, -6.2) * mm, "end": v(18.5, -6.24) * mm});
            skLineSegment(sketch, "E1378", {"start": v(18.5, -6.24) * mm, "end": v(18.67, -6.25) * mm});
            skLineSegment(sketch, "E1379", {"start": v(18.67, -6.25) * mm, "end": v(18.83, -6.26) * mm});
            skLineSegment(sketch, "E1380", {"start": v(18.83, -6.26) * mm, "end": v(18.98, -6.26) * mm});
            skLineSegment(sketch, "E1381", {"start": v(18.98, -6.26) * mm, "end": v(19.12, -6.26) * mm});
            skLineSegment(sketch, "E1382", {"start": v(19.12, -6.26) * mm, "end": v(19.25, -6.26) * mm});
            skLineSegment(sketch, "E1383", {"start": v(19.25, -6.26) * mm, "end": v(19.38, -6.25) * mm});
            skLineSegment(sketch, "E1384", {"start": v(19.38, -6.25) * mm, "end": v(19.5, -6.24) * mm});
            skLineSegment(sketch, "E1385", {"start": v(19.5, -6.24) * mm, "end": v(19.63, -6.23) * mm});
            skLineSegment(sketch, "E1386", {"start": v(19.63, -6.23) * mm, "end": v(19.75, -6.22) * mm});
            skLineSegment(sketch, "E1387", {"start": v(19.75, -6.22) * mm, "end": v(19.87, -6.2) * mm});
            skLineSegment(sketch, "E1388", {"start": v(19.87, -6.2) * mm, "end": v(20, -6.2) * mm});
            skLineSegment(sketch, "E1389", {"start": v(20, -6.2) * mm, "end": v(20.1, -6.18) * mm});
            skLineSegment(sketch, "E1390", {"start": v(20.1, -6.18) * mm, "end": v(20.22, -6.16) * mm});
            skLineSegment(sketch, "E1391", {"start": v(20.22, -6.16) * mm, "end": v(20.4, -5.5) * mm});
            skLineSegment(sketch, "E1392", {"start": v(20.4, -5.5) * mm, "end": v(20.32, -5.42) * mm});
            skLineSegment(sketch, "E1393", {"start": v(20.32, -5.42) * mm, "end": v(20.23, -5.35) * mm});
            skLineSegment(sketch, "E1394", {"start": v(20.23, -5.35) * mm, "end": v(20.14, -5.27) * mm});
            skLineSegment(sketch, "E1395", {"start": v(20.14, -5.27) * mm, "end": v(20.05, -5.2) * mm});
            skLineSegment(sketch, "E1396", {"start": v(20.05, -5.2) * mm, "end": v(19.95, -5.12) * mm});
            skLineSegment(sketch, "E1397", {"start": v(19.95, -5.12) * mm, "end": v(19.85, -5.05) * mm});
            skLineSegment(sketch, "E1398", {"start": v(19.85, -5.05) * mm, "end": v(19.75, -4.98) * mm});
            skLineSegment(sketch, "E1399", {"start": v(19.75, -4.98) * mm, "end": v(19.64, -4.9) * mm});
            skLineSegment(sketch, "E1400", {"start": v(19.64, -4.9) * mm, "end": v(19.53, -4.83) * mm});
            skLineSegment(sketch, "E1401", {"start": v(19.53, -4.83) * mm, "end": v(19.41, -4.76) * mm});
            skLineSegment(sketch, "E1402", {"start": v(19.41, -4.76) * mm, "end": v(19.29, -4.68) * mm});
            skLineSegment(sketch, "E1403", {"start": v(19.29, -4.68) * mm, "end": v(19.15, -4.6) * mm});
            skLineSegment(sketch, "E1404", {"start": v(19.15, -4.6) * mm, "end": v(18.99, -4.52) * mm});
            skLineSegment(sketch, "E1405", {"start": v(18.99, -4.52) * mm, "end": v(18.69, -4.38) * mm});
            skLineSegment(sketch, "E1406", {"start": v(18.69, -4.38) * mm, "end": v(18.67, -4.38) * mm});
            skLineSegment(sketch, "E1407", {"start": v(18.67, -4.38) * mm, "end": v(18.84, -3.6) * mm});
            skLineSegment(sketch, "E1408", {"start": v(18.84, -3.6) * mm, "end": v(18.85, -3.6) * mm});
            skLineSegment(sketch, "E1409", {"start": v(18.85, -3.6) * mm, "end": v(19.18, -3.6) * mm});
            skLineSegment(sketch, "E1410", {"start": v(19.18, -3.6) * mm, "end": v(19.36, -3.6) * mm});
            skLineSegment(sketch, "E1411", {"start": v(19.36, -3.6) * mm, "end": v(19.52, -3.58) * mm});
            skLineSegment(sketch, "E1412", {"start": v(19.52, -3.58) * mm, "end": v(19.67, -3.56) * mm});
            skLineSegment(sketch, "E1413", {"start": v(19.67, -3.56) * mm, "end": v(19.8, -3.54) * mm});
            skLineSegment(sketch, "E1414", {"start": v(19.8, -3.54) * mm, "end": v(19.94, -3.51) * mm});
            skLineSegment(sketch, "E1415", {"start": v(19.94, -3.51) * mm, "end": v(20.07, -3.5) * mm});
            skLineSegment(sketch, "E1416", {"start": v(20.07, -3.5) * mm, "end": v(20.19, -3.47) * mm});
            skLineSegment(sketch, "E1417", {"start": v(20.19, -3.47) * mm, "end": v(20.3, -3.44) * mm});
            skLineSegment(sketch, "E1418", {"start": v(20.3, -3.44) * mm, "end": v(20.43, -3.41) * mm});
            skLineSegment(sketch, "E1419", {"start": v(20.43, -3.41) * mm, "end": v(20.54, -3.38) * mm});
            skLineSegment(sketch, "E1420", {"start": v(20.54, -3.38) * mm, "end": v(20.66, -3.35) * mm});
            skLineSegment(sketch, "E1421", {"start": v(20.66, -3.35) * mm, "end": v(20.77, -3.32) * mm});
            skLineSegment(sketch, "E1422", {"start": v(20.77, -3.32) * mm, "end": v(20.88, -3.29) * mm});
            skLineSegment(sketch, "E1423", {"start": v(20.88, -3.29) * mm, "end": v(20.98, -2.6) * mm});
            skLineSegment(sketch, "E1424", {"start": v(20.98, -2.6) * mm, "end": v(20.88, -2.54) * mm});
            skLineSegment(sketch, "E1425", {"start": v(20.88, -2.54) * mm, "end": v(20.78, -2.48) * mm});
            skLineSegment(sketch, "E1426", {"start": v(20.78, -2.48) * mm, "end": v(20.68, -2.42) * mm});
            skLineSegment(sketch, "E1427", {"start": v(20.68, -2.42) * mm, "end": v(20.58, -2.36) * mm});
            skLineSegment(sketch, "E1428", {"start": v(20.58, -2.36) * mm, "end": v(20.47, -2.3) * mm});
            skLineSegment(sketch, "E1429", {"start": v(20.47, -2.3) * mm, "end": v(20.36, -2.24) * mm});
            skLineSegment(sketch, "E1430", {"start": v(20.36, -2.24) * mm, "end": v(20.25, -2.18) * mm});
            skLineSegment(sketch, "E1431", {"start": v(20.25, -2.18) * mm, "end": v(20.13, -2.12) * mm});
            skLineSegment(sketch, "E1432", {"start": v(20.13, -2.12) * mm, "end": v(20.01, -2.06) * mm});
            skLineSegment(sketch, "E1433", {"start": v(20.01, -2.06) * mm, "end": v(19.89, -2) * mm});
            skLineSegment(sketch, "E1434", {"start": v(19.89, -2) * mm, "end": v(19.75, -1.95) * mm});
            skLineSegment(sketch, "E1435", {"start": v(19.75, -1.95) * mm, "end": v(19.6, -1.89) * mm});
            skLineSegment(sketch, "E1436", {"start": v(19.6, -1.89) * mm, "end": v(19.43, -1.83) * mm});
            skLineSegment(sketch, "E1437", {"start": v(19.43, -1.83) * mm, "end": v(19.12, -1.74) * mm});
            skLineSegment(sketch, "E1438", {"start": v(19.12, -1.74) * mm, "end": v(19.1, -1.74) * mm});
            skLineSegment(sketch, "E1439", {"start": v(19.1, -1.74) * mm, "end": v(19.15, -0.94) * mm});
            skArc(sketch, "E1440", {"start": v(2.49, 0) * mm, "mid": v(-0.01, 2.5) * mm, "end": v(-2.51, 0) * mm});
            skArc(sketch, "E1441", {"start": v(-2.51, 0) * mm, "mid": v(-0.01, -2.5) * mm, "end": v(2.49, 0) * mm});
            skSolve(sketch);
        }
        {
            var Q0;
            Q0=makeQuery(id+"F0.imprint","IMPRINT",FACE,{"disambiguationData":[TD([[makeQuery(id+"F0.imprint","IMPRINT",EDGE,{"derivedFrom":sQuery(id+"F0.wireOp",EDGE,"E0")}),1.0]])]});
            var Q1;
            Q1=makeQuery(id+"F0.imprint","IMPRINT",FACE,{"disambiguationData":[TD([[makeQuery(id+"F0.imprint","IMPRINT",EDGE,{"derivedFrom":sQuery(id+"F0.wireOp",EDGE,"E1440")}),1.0]])]});
            extrude(context, id + "F1", {"entities" : qUnion([Q0, Q1]), "depth" : 5 * mm});
        }
    });
